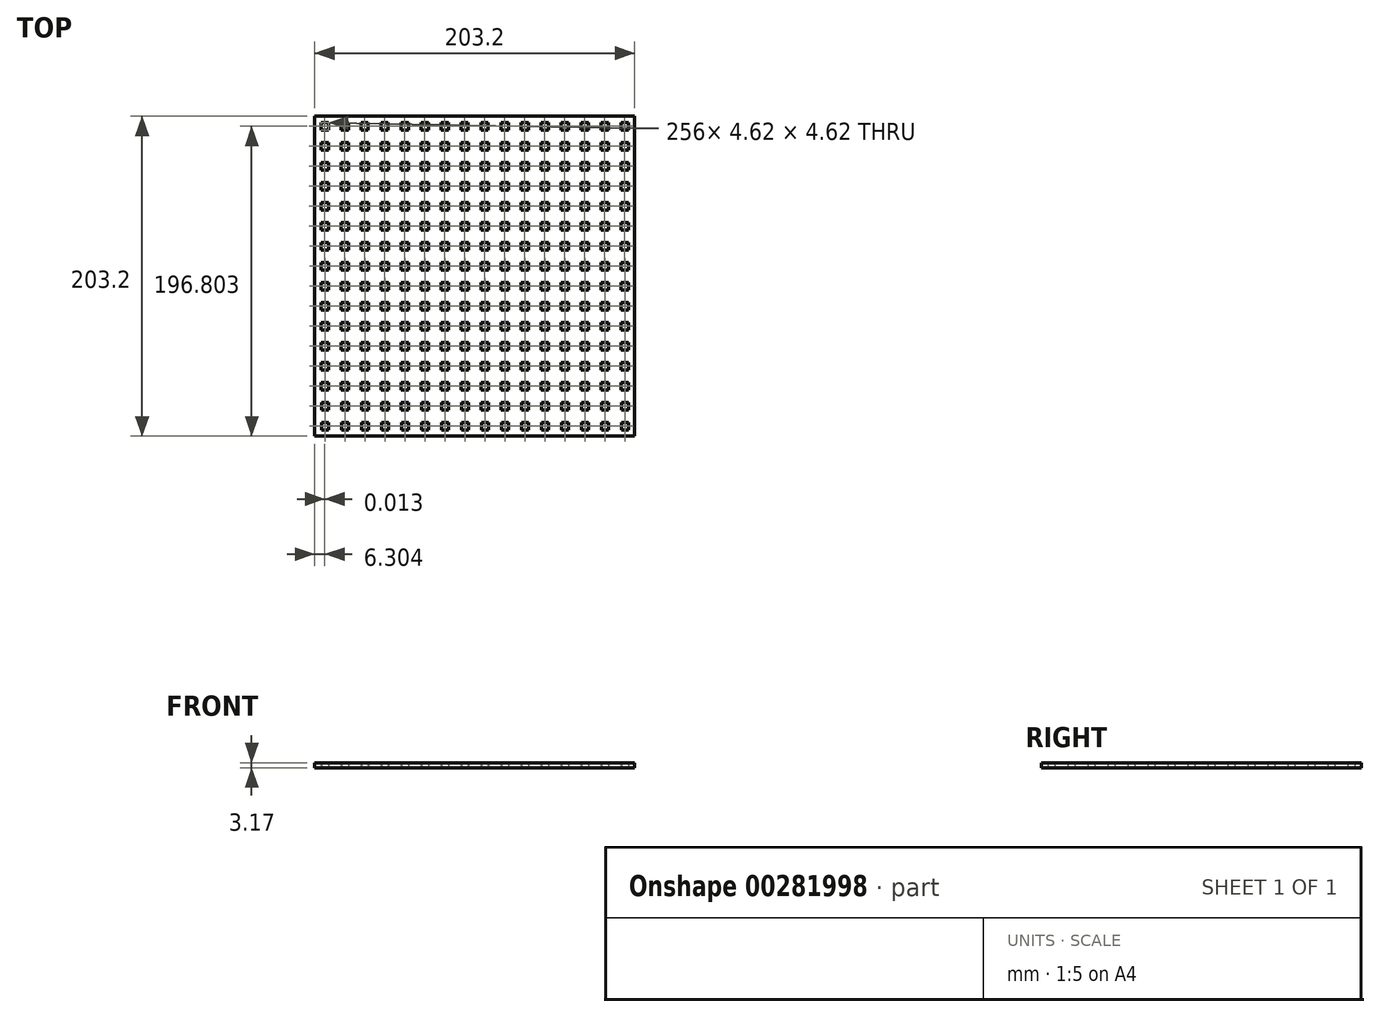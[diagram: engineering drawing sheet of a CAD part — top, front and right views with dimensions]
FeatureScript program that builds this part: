
annotation { "Feature Type Name" : "Feature", "Feature Type Description" : "" }
export const myFeature = defineFeature(function(context is Context, id is Id, definition is map)
    precondition{}
    {
        {
            var Q0;
            Q0=qCreatedBy(makeId("Top.planeOp"),FACE);
            var sketch = newSketch(context, id + "F0", { "sketchPlane" : qUnion([Q0])});
            skLineSegment(sketch, "E0.bottom", {"start": v(-83.26, 106.61) * mm, "end": v(119.94, 106.61) * mm});
            skLineSegment(sketch, "E0.top", {"start": v(-83.26, -96.59) * mm, "end": v(119.94, -96.59) * mm});
            skLineSegment(sketch, "E0.left", {"start": v(-83.26, 106.61) * mm, "end": v(-83.26, -96.59) * mm});
            skLineSegment(sketch, "E0.right", {"start": v(119.94, 106.61) * mm, "end": v(119.94, -96.59) * mm});
            skPoint(sketch, "E1", {"position": v(-79.27, 106.61) * mm});
            skPoint(sketch, "E2", {"position": v(-83.26, 102.52) * mm});
            skLineSegment(sketch, "E3.bottom", {"start": v(-79.27, 102.52) * mm, "end": v(-74.64, 102.52) * mm});
            skLineSegment(sketch, "E3.top", {"start": v(-79.27, 97.9) * mm, "end": v(-74.64, 97.9) * mm});
            skLineSegment(sketch, "E3.left", {"start": v(-79.27, 102.52) * mm, "end": v(-79.27, 97.9) * mm});
            skLineSegment(sketch, "E3.right", {"start": v(-74.64, 102.52) * mm, "end": v(-74.64, 97.9) * mm});
            skPoint(sketch, "E4", {"position": v(-76.96, 102.52) * mm});
            skPoint(sketch, "E5", {"position": v(-64.26, 102.52) * mm});
            skLineSegment(sketch, "E6.bottom", {"start": v(-66.57, 102.52) * mm, "end": v(-61.94, 102.52) * mm});
            skLineSegment(sketch, "E6.top", {"start": v(-66.57, 97.9) * mm, "end": v(-61.94, 97.9) * mm});
            skLineSegment(sketch, "E6.left", {"start": v(-66.57, 102.52) * mm, "end": v(-66.57, 97.9) * mm});
            skLineSegment(sketch, "E6.right", {"start": v(-61.94, 102.52) * mm, "end": v(-61.94, 97.9) * mm});
            skLineSegment(sketch, "E7.1.0.0", {"start": v(-53.87, 97.9) * mm, "end": v(-49.24, 97.9) * mm});
            skLineSegment(sketch, "E7.1.0.1", {"start": v(-36.54, 102.52) * mm, "end": v(-36.54, 97.9) * mm});
            skLineSegment(sketch, "E7.1.0.2", {"start": v(-41.17, 97.9) * mm, "end": v(-36.54, 97.9) * mm});
            skLineSegment(sketch, "E7.1.0.3", {"start": v(-41.17, 102.52) * mm, "end": v(-41.17, 97.9) * mm});
            skPoint(sketch, "E7.1.0.4", {"position": v(-51.56, 102.52) * mm});
            skPoint(sketch, "E7.1.0.5", {"position": v(-38.86, 102.52) * mm});
            skLineSegment(sketch, "E7.1.0.6", {"start": v(-53.87, 102.52) * mm, "end": v(-53.87, 97.9) * mm});
            skLineSegment(sketch, "E7.1.0.7", {"start": v(-49.24, 102.52) * mm, "end": v(-49.24, 97.9) * mm});
            skLineSegment(sketch, "E7.1.0.8", {"start": v(-41.17, 102.52) * mm, "end": v(-36.54, 102.52) * mm});
            skLineSegment(sketch, "E7.1.0.9", {"start": v(-53.87, 102.52) * mm, "end": v(-49.24, 102.52) * mm});
            skLineSegment(sketch, "E7.2.0.0", {"start": v(-28.47, 97.9) * mm, "end": v(-23.84, 97.9) * mm});
            skLineSegment(sketch, "E7.2.0.1", {"start": v(-11.14, 102.52) * mm, "end": v(-11.14, 97.9) * mm});
            skLineSegment(sketch, "E7.2.0.2", {"start": v(-15.77, 97.9) * mm, "end": v(-11.14, 97.9) * mm});
            skLineSegment(sketch, "E7.2.0.3", {"start": v(-15.77, 102.52) * mm, "end": v(-15.77, 97.9) * mm});
            skPoint(sketch, "E7.2.0.4", {"position": v(-26.16, 102.52) * mm});
            skPoint(sketch, "E7.2.0.5", {"position": v(-13.46, 102.52) * mm});
            skLineSegment(sketch, "E7.2.0.6", {"start": v(-28.47, 102.52) * mm, "end": v(-28.47, 97.9) * mm});
            skLineSegment(sketch, "E7.2.0.7", {"start": v(-23.84, 102.52) * mm, "end": v(-23.84, 97.9) * mm});
            skLineSegment(sketch, "E7.2.0.8", {"start": v(-15.77, 102.52) * mm, "end": v(-11.14, 102.52) * mm});
            skLineSegment(sketch, "E7.2.0.9", {"start": v(-28.47, 102.52) * mm, "end": v(-23.84, 102.52) * mm});
            skLineSegment(sketch, "E7.3.0.0", {"start": v(-3.07, 97.9) * mm, "end": v(1.56, 97.9) * mm});
            skLineSegment(sketch, "E7.3.0.1", {"start": v(14.26, 102.52) * mm, "end": v(14.26, 97.9) * mm});
            skLineSegment(sketch, "E7.3.0.2", {"start": v(9.63, 97.9) * mm, "end": v(14.26, 97.9) * mm});
            skLineSegment(sketch, "E7.3.0.3", {"start": v(9.63, 102.52) * mm, "end": v(9.63, 97.9) * mm});
            skPoint(sketch, "E7.3.0.4", {"position": v(-0.76, 102.52) * mm});
            skPoint(sketch, "E7.3.0.5", {"position": v(11.94, 102.52) * mm});
            skLineSegment(sketch, "E7.3.0.6", {"start": v(-3.07, 102.52) * mm, "end": v(-3.07, 97.9) * mm});
            skLineSegment(sketch, "E7.3.0.7", {"start": v(1.56, 102.52) * mm, "end": v(1.56, 97.9) * mm});
            skLineSegment(sketch, "E7.3.0.8", {"start": v(9.63, 102.52) * mm, "end": v(14.26, 102.52) * mm});
            skLineSegment(sketch, "E7.3.0.9", {"start": v(-3.07, 102.52) * mm, "end": v(1.56, 102.52) * mm});
            skLineSegment(sketch, "E7.4.0.0", {"start": v(22.33, 97.9) * mm, "end": v(26.96, 97.9) * mm});
            skLineSegment(sketch, "E7.4.0.1", {"start": v(39.66, 102.52) * mm, "end": v(39.66, 97.9) * mm});
            skLineSegment(sketch, "E7.4.0.2", {"start": v(35.03, 97.9) * mm, "end": v(39.66, 97.9) * mm});
            skLineSegment(sketch, "E7.4.0.3", {"start": v(35.03, 102.52) * mm, "end": v(35.03, 97.9) * mm});
            skPoint(sketch, "E7.4.0.4", {"position": v(24.64, 102.52) * mm});
            skPoint(sketch, "E7.4.0.5", {"position": v(37.34, 102.52) * mm});
            skLineSegment(sketch, "E7.4.0.6", {"start": v(22.33, 102.52) * mm, "end": v(22.33, 97.9) * mm});
            skLineSegment(sketch, "E7.4.0.7", {"start": v(26.96, 102.52) * mm, "end": v(26.96, 97.9) * mm});
            skLineSegment(sketch, "E7.4.0.8", {"start": v(35.03, 102.52) * mm, "end": v(39.66, 102.52) * mm});
            skLineSegment(sketch, "E7.4.0.9", {"start": v(22.33, 102.52) * mm, "end": v(26.96, 102.52) * mm});
            skLineSegment(sketch, "E7.5.0.0", {"start": v(47.73, 97.9) * mm, "end": v(52.36, 97.9) * mm});
            skLineSegment(sketch, "E7.5.0.1", {"start": v(65.06, 102.52) * mm, "end": v(65.06, 97.9) * mm});
            skLineSegment(sketch, "E7.5.0.2", {"start": v(60.43, 97.9) * mm, "end": v(65.06, 97.9) * mm});
            skLineSegment(sketch, "E7.5.0.3", {"start": v(60.43, 102.52) * mm, "end": v(60.43, 97.9) * mm});
            skPoint(sketch, "E7.5.0.4", {"position": v(50.04, 102.52) * mm});
            skPoint(sketch, "E7.5.0.5", {"position": v(62.74, 102.52) * mm});
            skLineSegment(sketch, "E7.5.0.6", {"start": v(47.73, 102.52) * mm, "end": v(47.73, 97.9) * mm});
            skLineSegment(sketch, "E7.5.0.7", {"start": v(52.36, 102.52) * mm, "end": v(52.36, 97.9) * mm});
            skLineSegment(sketch, "E7.5.0.8", {"start": v(60.43, 102.52) * mm, "end": v(65.06, 102.52) * mm});
            skLineSegment(sketch, "E7.5.0.9", {"start": v(47.73, 102.52) * mm, "end": v(52.36, 102.52) * mm});
            skLineSegment(sketch, "E7.6.0.0", {"start": v(73.13, 97.9) * mm, "end": v(77.76, 97.9) * mm});
            skLineSegment(sketch, "E7.6.0.1", {"start": v(90.46, 102.52) * mm, "end": v(90.46, 97.9) * mm});
            skLineSegment(sketch, "E7.6.0.2", {"start": v(85.83, 97.9) * mm, "end": v(90.46, 97.9) * mm});
            skLineSegment(sketch, "E7.6.0.3", {"start": v(85.83, 102.52) * mm, "end": v(85.83, 97.9) * mm});
            skPoint(sketch, "E7.6.0.4", {"position": v(75.44, 102.52) * mm});
            skPoint(sketch, "E7.6.0.5", {"position": v(88.14, 102.52) * mm});
            skLineSegment(sketch, "E7.6.0.6", {"start": v(73.13, 102.52) * mm, "end": v(73.13, 97.9) * mm});
            skLineSegment(sketch, "E7.6.0.7", {"start": v(77.76, 102.52) * mm, "end": v(77.76, 97.9) * mm});
            skLineSegment(sketch, "E7.6.0.8", {"start": v(85.83, 102.52) * mm, "end": v(90.46, 102.52) * mm});
            skLineSegment(sketch, "E7.6.0.9", {"start": v(73.13, 102.52) * mm, "end": v(77.76, 102.52) * mm});
            skLineSegment(sketch, "E7.7.0.0", {"start": v(98.53, 97.9) * mm, "end": v(103.16, 97.9) * mm});
            skLineSegment(sketch, "E7.7.0.1", {"start": v(115.86, 102.52) * mm, "end": v(115.86, 97.9) * mm});
            skLineSegment(sketch, "E7.7.0.2", {"start": v(111.23, 97.9) * mm, "end": v(115.86, 97.9) * mm});
            skLineSegment(sketch, "E7.7.0.3", {"start": v(111.23, 102.52) * mm, "end": v(111.23, 97.9) * mm});
            skPoint(sketch, "E7.7.0.4", {"position": v(100.84, 102.52) * mm});
            skPoint(sketch, "E7.7.0.5", {"position": v(113.54, 102.52) * mm});
            skLineSegment(sketch, "E7.7.0.6", {"start": v(98.53, 102.52) * mm, "end": v(98.53, 97.9) * mm});
            skLineSegment(sketch, "E7.7.0.7", {"start": v(103.16, 102.52) * mm, "end": v(103.16, 97.9) * mm});
            skLineSegment(sketch, "E7.7.0.8", {"start": v(111.23, 102.52) * mm, "end": v(115.86, 102.52) * mm});
            skLineSegment(sketch, "E7.7.0.9", {"start": v(98.53, 102.52) * mm, "end": v(103.16, 102.52) * mm});
            skLineSegment(sketch, "E7.direction1", {"start": v(-76.96, 102.52) * mm, "end": v(-51.56, 102.52) * mm, "construction": true});
            skPoint(sketch, "E8", {"position": v(-79.27, 100.21) * mm});
            skPoint(sketch, "E9.1.0.0", {"position": v(-79.25, 87.51) * mm});
            skPoint(sketch, "E9.1.0.1", {"position": v(88.16, 89.82) * mm});
            skPoint(sketch, "E9.1.0.2", {"position": v(37.36, 89.82) * mm});
            skPoint(sketch, "E9.1.0.3", {"position": v(-51.54, 89.82) * mm});
            skPoint(sketch, "E9.1.0.4", {"position": v(113.56, 89.82) * mm});
            skPoint(sketch, "E9.1.0.5", {"position": v(-64.24, 89.82) * mm});
            skPoint(sketch, "E9.1.0.6", {"position": v(24.66, 89.82) * mm});
            skPoint(sketch, "E9.1.0.7", {"position": v(11.96, 89.82) * mm});
            skLineSegment(sketch, "E9.1.0.8", {"start": v(-76.94, 89.82) * mm, "end": v(-51.54, 89.82) * mm, "construction": true});
            skPoint(sketch, "E9.1.0.9", {"position": v(-76.94, 89.82) * mm});
            skPoint(sketch, "E9.1.0.10", {"position": v(-13.44, 89.82) * mm});
            skPoint(sketch, "E9.1.0.11", {"position": v(50.06, 89.82) * mm});
            skPoint(sketch, "E9.1.0.12", {"position": v(-38.84, 89.82) * mm});
            skPoint(sketch, "E9.1.0.13", {"position": v(62.76, 89.82) * mm});
            skPoint(sketch, "E9.1.0.14", {"position": v(-26.14, 89.82) * mm});
            skPoint(sketch, "E9.1.0.15", {"position": v(75.46, 89.82) * mm});
            skPoint(sketch, "E9.1.0.16", {"position": v(-0.74, 89.82) * mm});
            skPoint(sketch, "E9.1.0.17", {"position": v(100.86, 89.82) * mm});
            skLineSegment(sketch, "E9.1.0.18", {"start": v(90.47, 89.82) * mm, "end": v(90.47, 85.2) * mm});
            skLineSegment(sketch, "E9.1.0.19", {"start": v(47.75, 89.82) * mm, "end": v(47.75, 85.2) * mm});
            skLineSegment(sketch, "E9.1.0.20", {"start": v(-28.45, 89.82) * mm, "end": v(-28.45, 85.2) * mm});
            skLineSegment(sketch, "E9.1.0.21", {"start": v(73.15, 89.82) * mm, "end": v(73.15, 85.2) * mm});
            skLineSegment(sketch, "E9.1.0.22", {"start": v(9.65, 85.2) * mm, "end": v(14.27, 85.2) * mm});
            skLineSegment(sketch, "E9.1.0.23", {"start": v(98.55, 89.82) * mm, "end": v(98.55, 85.2) * mm});
            skLineSegment(sketch, "E9.1.0.24", {"start": v(39.67, 89.82) * mm, "end": v(39.67, 85.2) * mm});
            skLineSegment(sketch, "E9.1.0.25", {"start": v(-15.75, 89.82) * mm, "end": v(-15.75, 85.2) * mm});
            skLineSegment(sketch, "E9.1.0.26", {"start": v(60.45, 85.2) * mm, "end": v(65.07, 85.2) * mm});
            skLineSegment(sketch, "E9.1.0.27", {"start": v(35.05, 89.82) * mm, "end": v(35.05, 85.2) * mm});
            skLineSegment(sketch, "E9.1.0.28", {"start": v(85.85, 89.82) * mm, "end": v(85.85, 85.2) * mm});
            skLineSegment(sketch, "E9.1.0.29", {"start": v(-53.85, 85.2) * mm, "end": v(-49.23, 85.2) * mm});
            skLineSegment(sketch, "E9.1.0.30", {"start": v(-66.55, 89.82) * mm, "end": v(-61.93, 89.82) * mm});
            skLineSegment(sketch, "E9.1.0.31", {"start": v(111.25, 85.2) * mm, "end": v(115.87, 85.2) * mm});
            skLineSegment(sketch, "E9.1.0.32", {"start": v(-74.63, 89.82) * mm, "end": v(-74.63, 85.2) * mm});
            skLineSegment(sketch, "E9.1.0.33", {"start": v(-79.25, 89.82) * mm, "end": v(-79.25, 85.2) * mm});
            skLineSegment(sketch, "E9.1.0.34", {"start": v(-79.25, 89.82) * mm, "end": v(-74.63, 89.82) * mm});
            skLineSegment(sketch, "E9.1.0.35", {"start": v(-41.15, 89.82) * mm, "end": v(-41.15, 85.2) * mm});
            skLineSegment(sketch, "E9.1.0.36", {"start": v(-11.13, 89.82) * mm, "end": v(-11.13, 85.2) * mm});
            skLineSegment(sketch, "E9.1.0.37", {"start": v(-3.05, 85.2) * mm, "end": v(1.57, 85.2) * mm});
            skLineSegment(sketch, "E9.1.0.38", {"start": v(47.75, 85.2) * mm, "end": v(52.37, 85.2) * mm});
            skLineSegment(sketch, "E9.1.0.39", {"start": v(98.55, 85.2) * mm, "end": v(103.17, 85.2) * mm});
            skLineSegment(sketch, "E9.1.0.40", {"start": v(9.65, 89.82) * mm, "end": v(14.27, 89.82) * mm});
            skLineSegment(sketch, "E9.1.0.41", {"start": v(14.27, 89.82) * mm, "end": v(14.27, 85.2) * mm});
            skLineSegment(sketch, "E9.1.0.42", {"start": v(22.35, 85.2) * mm, "end": v(26.97, 85.2) * mm});
            skLineSegment(sketch, "E9.1.0.43", {"start": v(73.15, 85.2) * mm, "end": v(77.77, 85.2) * mm});
            skLineSegment(sketch, "E9.1.0.44", {"start": v(115.87, 89.82) * mm, "end": v(115.87, 85.2) * mm});
            skLineSegment(sketch, "E9.1.0.45", {"start": v(60.45, 89.82) * mm, "end": v(65.07, 89.82) * mm});
            skLineSegment(sketch, "E9.1.0.46", {"start": v(111.25, 89.82) * mm, "end": v(115.87, 89.82) * mm});
            skLineSegment(sketch, "E9.1.0.47", {"start": v(-15.75, 89.82) * mm, "end": v(-11.13, 89.82) * mm});
            skLineSegment(sketch, "E9.1.0.48", {"start": v(35.05, 89.82) * mm, "end": v(39.67, 89.82) * mm});
            skLineSegment(sketch, "E9.1.0.49", {"start": v(-23.83, 89.82) * mm, "end": v(-23.83, 85.2) * mm});
            skLineSegment(sketch, "E9.1.0.50", {"start": v(85.85, 89.82) * mm, "end": v(90.47, 89.82) * mm});
            skLineSegment(sketch, "E9.1.0.51", {"start": v(65.07, 89.82) * mm, "end": v(65.07, 85.2) * mm});
            skLineSegment(sketch, "E9.1.0.52", {"start": v(52.37, 89.82) * mm, "end": v(52.37, 85.2) * mm});
            skLineSegment(sketch, "E9.1.0.53", {"start": v(103.17, 89.82) * mm, "end": v(103.17, 85.2) * mm});
            skLineSegment(sketch, "E9.1.0.54", {"start": v(-15.75, 85.2) * mm, "end": v(-11.13, 85.2) * mm});
            skLineSegment(sketch, "E9.1.0.55", {"start": v(111.25, 89.82) * mm, "end": v(111.25, 85.2) * mm});
            skLineSegment(sketch, "E9.1.0.56", {"start": v(60.45, 89.82) * mm, "end": v(60.45, 85.2) * mm});
            skLineSegment(sketch, "E9.1.0.57", {"start": v(85.85, 85.2) * mm, "end": v(90.47, 85.2) * mm});
            skLineSegment(sketch, "E9.1.0.58", {"start": v(35.05, 85.2) * mm, "end": v(39.67, 85.2) * mm});
            skLineSegment(sketch, "E9.1.0.59", {"start": v(9.65, 89.82) * mm, "end": v(9.65, 85.2) * mm});
            skLineSegment(sketch, "E9.1.0.60", {"start": v(-36.53, 89.82) * mm, "end": v(-36.53, 85.2) * mm});
            skLineSegment(sketch, "E9.1.0.61", {"start": v(-41.15, 85.2) * mm, "end": v(-36.53, 85.2) * mm});
            skLineSegment(sketch, "E9.1.0.62", {"start": v(-79.25, 85.2) * mm, "end": v(-74.63, 85.2) * mm});
            skLineSegment(sketch, "E9.1.0.63", {"start": v(-66.55, 85.2) * mm, "end": v(-61.93, 85.2) * mm});
            skLineSegment(sketch, "E9.1.0.64", {"start": v(-66.55, 89.82) * mm, "end": v(-66.55, 85.2) * mm});
            skLineSegment(sketch, "E9.1.0.65", {"start": v(-61.93, 89.82) * mm, "end": v(-61.93, 85.2) * mm});
            skLineSegment(sketch, "E9.1.0.66", {"start": v(-53.85, 89.82) * mm, "end": v(-53.85, 85.2) * mm});
            skLineSegment(sketch, "E9.1.0.67", {"start": v(-3.05, 89.82) * mm, "end": v(-3.05, 85.2) * mm});
            skLineSegment(sketch, "E9.1.0.68", {"start": v(22.35, 89.82) * mm, "end": v(22.35, 85.2) * mm});
            skLineSegment(sketch, "E9.1.0.69", {"start": v(-49.23, 89.82) * mm, "end": v(-49.23, 85.2) * mm});
            skLineSegment(sketch, "E9.1.0.70", {"start": v(1.57, 89.82) * mm, "end": v(1.57, 85.2) * mm});
            skLineSegment(sketch, "E9.1.0.71", {"start": v(77.77, 89.82) * mm, "end": v(77.77, 85.2) * mm});
            skLineSegment(sketch, "E9.1.0.72", {"start": v(26.97, 89.82) * mm, "end": v(26.97, 85.2) * mm});
            skLineSegment(sketch, "E9.1.0.73", {"start": v(-41.15, 89.82) * mm, "end": v(-36.53, 89.82) * mm});
            skLineSegment(sketch, "E9.1.0.74", {"start": v(-28.45, 85.2) * mm, "end": v(-23.83, 85.2) * mm});
            skLineSegment(sketch, "E9.1.0.75", {"start": v(-28.45, 89.82) * mm, "end": v(-23.83, 89.82) * mm});
            skLineSegment(sketch, "E9.1.0.76", {"start": v(22.35, 89.82) * mm, "end": v(26.97, 89.82) * mm});
            skLineSegment(sketch, "E9.1.0.77", {"start": v(73.15, 89.82) * mm, "end": v(77.77, 89.82) * mm});
            skLineSegment(sketch, "E9.1.0.78", {"start": v(-3.05, 89.82) * mm, "end": v(1.57, 89.82) * mm});
            skLineSegment(sketch, "E9.1.0.79", {"start": v(47.75, 89.82) * mm, "end": v(52.37, 89.82) * mm});
            skLineSegment(sketch, "E9.1.0.80", {"start": v(98.55, 89.82) * mm, "end": v(103.17, 89.82) * mm});
            skLineSegment(sketch, "E9.1.0.81", {"start": v(-53.85, 89.82) * mm, "end": v(-49.23, 89.82) * mm});
            skPoint(sketch, "E9.2.0.0", {"position": v(-79.24, 74.81) * mm});
            skPoint(sketch, "E9.2.0.1", {"position": v(88.17, 77.12) * mm});
            skPoint(sketch, "E9.2.0.2", {"position": v(37.37, 77.12) * mm});
            skPoint(sketch, "E9.2.0.3", {"position": v(-51.53, 77.12) * mm});
            skPoint(sketch, "E9.2.0.4", {"position": v(113.57, 77.12) * mm});
            skPoint(sketch, "E9.2.0.5", {"position": v(-64.23, 77.12) * mm});
            skPoint(sketch, "E9.2.0.6", {"position": v(24.67, 77.12) * mm});
            skPoint(sketch, "E9.2.0.7", {"position": v(11.97, 77.12) * mm});
            skLineSegment(sketch, "E9.2.0.8", {"start": v(-76.93, 77.12) * mm, "end": v(-51.53, 77.12) * mm, "construction": true});
            skPoint(sketch, "E9.2.0.9", {"position": v(-76.93, 77.12) * mm});
            skPoint(sketch, "E9.2.0.10", {"position": v(-13.43, 77.12) * mm});
            skPoint(sketch, "E9.2.0.11", {"position": v(50.07, 77.12) * mm});
            skPoint(sketch, "E9.2.0.12", {"position": v(-38.83, 77.12) * mm});
            skPoint(sketch, "E9.2.0.13", {"position": v(62.77, 77.12) * mm});
            skPoint(sketch, "E9.2.0.14", {"position": v(-26.13, 77.12) * mm});
            skPoint(sketch, "E9.2.0.15", {"position": v(75.47, 77.12) * mm});
            skPoint(sketch, "E9.2.0.16", {"position": v(-0.73, 77.12) * mm});
            skPoint(sketch, "E9.2.0.17", {"position": v(100.87, 77.12) * mm});
            skLineSegment(sketch, "E9.2.0.18", {"start": v(90.48, 77.12) * mm, "end": v(90.48, 72.5) * mm});
            skLineSegment(sketch, "E9.2.0.19", {"start": v(47.76, 77.12) * mm, "end": v(47.76, 72.5) * mm});
            skLineSegment(sketch, "E9.2.0.20", {"start": v(-28.44, 77.12) * mm, "end": v(-28.44, 72.5) * mm});
            skLineSegment(sketch, "E9.2.0.21", {"start": v(73.16, 77.12) * mm, "end": v(73.16, 72.5) * mm});
            skLineSegment(sketch, "E9.2.0.22", {"start": v(9.66, 72.5) * mm, "end": v(14.28, 72.5) * mm});
            skLineSegment(sketch, "E9.2.0.23", {"start": v(98.56, 77.12) * mm, "end": v(98.56, 72.5) * mm});
            skLineSegment(sketch, "E9.2.0.24", {"start": v(39.68, 77.12) * mm, "end": v(39.68, 72.5) * mm});
            skLineSegment(sketch, "E9.2.0.25", {"start": v(-15.74, 77.12) * mm, "end": v(-15.74, 72.5) * mm});
            skLineSegment(sketch, "E9.2.0.26", {"start": v(60.46, 72.5) * mm, "end": v(65.08, 72.5) * mm});
            skLineSegment(sketch, "E9.2.0.27", {"start": v(35.06, 77.12) * mm, "end": v(35.06, 72.5) * mm});
            skLineSegment(sketch, "E9.2.0.28", {"start": v(85.86, 77.12) * mm, "end": v(85.86, 72.5) * mm});
            skLineSegment(sketch, "E9.2.0.29", {"start": v(-53.84, 72.5) * mm, "end": v(-49.22, 72.5) * mm});
            skLineSegment(sketch, "E9.2.0.30", {"start": v(-66.54, 77.12) * mm, "end": v(-61.92, 77.12) * mm});
            skLineSegment(sketch, "E9.2.0.31", {"start": v(111.26, 72.5) * mm, "end": v(115.88, 72.5) * mm});
            skLineSegment(sketch, "E9.2.0.32", {"start": v(-74.62, 77.12) * mm, "end": v(-74.62, 72.5) * mm});
            skLineSegment(sketch, "E9.2.0.33", {"start": v(-79.24, 77.12) * mm, "end": v(-79.24, 72.5) * mm});
            skLineSegment(sketch, "E9.2.0.34", {"start": v(-79.24, 77.12) * mm, "end": v(-74.62, 77.12) * mm});
            skLineSegment(sketch, "E9.2.0.35", {"start": v(-41.14, 77.12) * mm, "end": v(-41.14, 72.5) * mm});
            skLineSegment(sketch, "E9.2.0.36", {"start": v(-11.12, 77.12) * mm, "end": v(-11.12, 72.5) * mm});
            skLineSegment(sketch, "E9.2.0.37", {"start": v(-3.04, 72.5) * mm, "end": v(1.58, 72.5) * mm});
            skLineSegment(sketch, "E9.2.0.38", {"start": v(47.76, 72.5) * mm, "end": v(52.38, 72.5) * mm});
            skLineSegment(sketch, "E9.2.0.39", {"start": v(98.56, 72.5) * mm, "end": v(103.18, 72.5) * mm});
            skLineSegment(sketch, "E9.2.0.40", {"start": v(9.66, 77.12) * mm, "end": v(14.28, 77.12) * mm});
            skLineSegment(sketch, "E9.2.0.41", {"start": v(14.28, 77.12) * mm, "end": v(14.28, 72.5) * mm});
            skLineSegment(sketch, "E9.2.0.42", {"start": v(22.36, 72.5) * mm, "end": v(26.98, 72.5) * mm});
            skLineSegment(sketch, "E9.2.0.43", {"start": v(73.16, 72.5) * mm, "end": v(77.78, 72.5) * mm});
            skLineSegment(sketch, "E9.2.0.44", {"start": v(115.88, 77.12) * mm, "end": v(115.88, 72.5) * mm});
            skLineSegment(sketch, "E9.2.0.45", {"start": v(60.46, 77.12) * mm, "end": v(65.08, 77.12) * mm});
            skLineSegment(sketch, "E9.2.0.46", {"start": v(111.26, 77.12) * mm, "end": v(115.88, 77.12) * mm});
            skLineSegment(sketch, "E9.2.0.47", {"start": v(-15.74, 77.12) * mm, "end": v(-11.12, 77.12) * mm});
            skLineSegment(sketch, "E9.2.0.48", {"start": v(35.06, 77.12) * mm, "end": v(39.68, 77.12) * mm});
            skLineSegment(sketch, "E9.2.0.49", {"start": v(-23.82, 77.12) * mm, "end": v(-23.82, 72.5) * mm});
            skLineSegment(sketch, "E9.2.0.50", {"start": v(85.86, 77.12) * mm, "end": v(90.48, 77.12) * mm});
            skLineSegment(sketch, "E9.2.0.51", {"start": v(65.08, 77.12) * mm, "end": v(65.08, 72.5) * mm});
            skLineSegment(sketch, "E9.2.0.52", {"start": v(52.38, 77.12) * mm, "end": v(52.38, 72.5) * mm});
            skLineSegment(sketch, "E9.2.0.53", {"start": v(103.18, 77.12) * mm, "end": v(103.18, 72.5) * mm});
            skLineSegment(sketch, "E9.2.0.54", {"start": v(-15.74, 72.5) * mm, "end": v(-11.12, 72.5) * mm});
            skLineSegment(sketch, "E9.2.0.55", {"start": v(111.26, 77.12) * mm, "end": v(111.26, 72.5) * mm});
            skLineSegment(sketch, "E9.2.0.56", {"start": v(60.46, 77.12) * mm, "end": v(60.46, 72.5) * mm});
            skLineSegment(sketch, "E9.2.0.57", {"start": v(85.86, 72.5) * mm, "end": v(90.48, 72.5) * mm});
            skLineSegment(sketch, "E9.2.0.58", {"start": v(35.06, 72.5) * mm, "end": v(39.68, 72.5) * mm});
            skLineSegment(sketch, "E9.2.0.59", {"start": v(9.66, 77.12) * mm, "end": v(9.66, 72.5) * mm});
            skLineSegment(sketch, "E9.2.0.60", {"start": v(-36.52, 77.12) * mm, "end": v(-36.52, 72.5) * mm});
            skLineSegment(sketch, "E9.2.0.61", {"start": v(-41.14, 72.5) * mm, "end": v(-36.52, 72.5) * mm});
            skLineSegment(sketch, "E9.2.0.62", {"start": v(-79.24, 72.5) * mm, "end": v(-74.62, 72.5) * mm});
            skLineSegment(sketch, "E9.2.0.63", {"start": v(-66.54, 72.5) * mm, "end": v(-61.92, 72.5) * mm});
            skLineSegment(sketch, "E9.2.0.64", {"start": v(-66.54, 77.12) * mm, "end": v(-66.54, 72.5) * mm});
            skLineSegment(sketch, "E9.2.0.65", {"start": v(-61.92, 77.12) * mm, "end": v(-61.92, 72.5) * mm});
            skLineSegment(sketch, "E9.2.0.66", {"start": v(-53.84, 77.12) * mm, "end": v(-53.84, 72.5) * mm});
            skLineSegment(sketch, "E9.2.0.67", {"start": v(-3.04, 77.12) * mm, "end": v(-3.04, 72.5) * mm});
            skLineSegment(sketch, "E9.2.0.68", {"start": v(22.36, 77.12) * mm, "end": v(22.36, 72.5) * mm});
            skLineSegment(sketch, "E9.2.0.69", {"start": v(-49.22, 77.12) * mm, "end": v(-49.22, 72.5) * mm});
            skLineSegment(sketch, "E9.2.0.70", {"start": v(1.58, 77.12) * mm, "end": v(1.58, 72.5) * mm});
            skLineSegment(sketch, "E9.2.0.71", {"start": v(77.78, 77.12) * mm, "end": v(77.78, 72.5) * mm});
            skLineSegment(sketch, "E9.2.0.72", {"start": v(26.98, 77.12) * mm, "end": v(26.98, 72.5) * mm});
            skLineSegment(sketch, "E9.2.0.73", {"start": v(-41.14, 77.12) * mm, "end": v(-36.52, 77.12) * mm});
            skLineSegment(sketch, "E9.2.0.74", {"start": v(-28.44, 72.5) * mm, "end": v(-23.82, 72.5) * mm});
            skLineSegment(sketch, "E9.2.0.75", {"start": v(-28.44, 77.12) * mm, "end": v(-23.82, 77.12) * mm});
            skLineSegment(sketch, "E9.2.0.76", {"start": v(22.36, 77.12) * mm, "end": v(26.98, 77.12) * mm});
            skLineSegment(sketch, "E9.2.0.77", {"start": v(73.16, 77.12) * mm, "end": v(77.78, 77.12) * mm});
            skLineSegment(sketch, "E9.2.0.78", {"start": v(-3.04, 77.12) * mm, "end": v(1.58, 77.12) * mm});
            skLineSegment(sketch, "E9.2.0.79", {"start": v(47.76, 77.12) * mm, "end": v(52.38, 77.12) * mm});
            skLineSegment(sketch, "E9.2.0.80", {"start": v(98.56, 77.12) * mm, "end": v(103.18, 77.12) * mm});
            skLineSegment(sketch, "E9.2.0.81", {"start": v(-53.84, 77.12) * mm, "end": v(-49.22, 77.12) * mm});
            skPoint(sketch, "E9.3.0.0", {"position": v(-79.23, 62.11) * mm});
            skPoint(sketch, "E9.3.0.1", {"position": v(88.18, 64.42) * mm});
            skPoint(sketch, "E9.3.0.2", {"position": v(37.38, 64.42) * mm});
            skPoint(sketch, "E9.3.0.3", {"position": v(-51.52, 64.42) * mm});
            skPoint(sketch, "E9.3.0.4", {"position": v(113.58, 64.42) * mm});
            skPoint(sketch, "E9.3.0.5", {"position": v(-64.22, 64.42) * mm});
            skPoint(sketch, "E9.3.0.6", {"position": v(24.68, 64.42) * mm});
            skPoint(sketch, "E9.3.0.7", {"position": v(11.98, 64.42) * mm});
            skLineSegment(sketch, "E9.3.0.8", {"start": v(-76.92, 64.42) * mm, "end": v(-51.52, 64.42) * mm, "construction": true});
            skPoint(sketch, "E9.3.0.9", {"position": v(-76.92, 64.42) * mm});
            skPoint(sketch, "E9.3.0.10", {"position": v(-13.42, 64.42) * mm});
            skPoint(sketch, "E9.3.0.11", {"position": v(50.08, 64.42) * mm});
            skPoint(sketch, "E9.3.0.12", {"position": v(-38.82, 64.42) * mm});
            skPoint(sketch, "E9.3.0.13", {"position": v(62.78, 64.42) * mm});
            skPoint(sketch, "E9.3.0.14", {"position": v(-26.12, 64.42) * mm});
            skPoint(sketch, "E9.3.0.15", {"position": v(75.48, 64.42) * mm});
            skPoint(sketch, "E9.3.0.16", {"position": v(-0.72, 64.42) * mm});
            skPoint(sketch, "E9.3.0.17", {"position": v(100.88, 64.42) * mm});
            skLineSegment(sketch, "E9.3.0.18", {"start": v(90.5, 64.42) * mm, "end": v(90.5, 59.8) * mm});
            skLineSegment(sketch, "E9.3.0.19", {"start": v(47.77, 64.42) * mm, "end": v(47.77, 59.8) * mm});
            skLineSegment(sketch, "E9.3.0.20", {"start": v(-28.43, 64.42) * mm, "end": v(-28.43, 59.8) * mm});
            skLineSegment(sketch, "E9.3.0.21", {"start": v(73.17, 64.42) * mm, "end": v(73.17, 59.8) * mm});
            skLineSegment(sketch, "E9.3.0.22", {"start": v(9.67, 59.8) * mm, "end": v(14.3, 59.8) * mm});
            skLineSegment(sketch, "E9.3.0.23", {"start": v(98.57, 64.42) * mm, "end": v(98.57, 59.8) * mm});
            skLineSegment(sketch, "E9.3.0.24", {"start": v(39.7, 64.42) * mm, "end": v(39.7, 59.8) * mm});
            skLineSegment(sketch, "E9.3.0.25", {"start": v(-15.73, 64.42) * mm, "end": v(-15.73, 59.8) * mm});
            skLineSegment(sketch, "E9.3.0.26", {"start": v(60.47, 59.8) * mm, "end": v(65.1, 59.8) * mm});
            skLineSegment(sketch, "E9.3.0.27", {"start": v(35.07, 64.42) * mm, "end": v(35.07, 59.8) * mm});
            skLineSegment(sketch, "E9.3.0.28", {"start": v(85.87, 64.42) * mm, "end": v(85.87, 59.8) * mm});
            skLineSegment(sketch, "E9.3.0.29", {"start": v(-53.83, 59.8) * mm, "end": v(-49.2, 59.8) * mm});
            skLineSegment(sketch, "E9.3.0.30", {"start": v(-66.53, 64.42) * mm, "end": v(-61.9, 64.42) * mm});
            skLineSegment(sketch, "E9.3.0.31", {"start": v(111.27, 59.8) * mm, "end": v(115.9, 59.8) * mm});
            skLineSegment(sketch, "E9.3.0.32", {"start": v(-74.6, 64.42) * mm, "end": v(-74.6, 59.8) * mm});
            skLineSegment(sketch, "E9.3.0.33", {"start": v(-79.23, 64.42) * mm, "end": v(-79.23, 59.8) * mm});
            skLineSegment(sketch, "E9.3.0.34", {"start": v(-79.23, 64.42) * mm, "end": v(-74.6, 64.42) * mm});
            skLineSegment(sketch, "E9.3.0.35", {"start": v(-41.13, 64.42) * mm, "end": v(-41.13, 59.8) * mm});
            skLineSegment(sketch, "E9.3.0.36", {"start": v(-11.1, 64.42) * mm, "end": v(-11.1, 59.8) * mm});
            skLineSegment(sketch, "E9.3.0.37", {"start": v(-3.03, 59.8) * mm, "end": v(1.6, 59.8) * mm});
            skLineSegment(sketch, "E9.3.0.38", {"start": v(47.77, 59.8) * mm, "end": v(52.4, 59.8) * mm});
            skLineSegment(sketch, "E9.3.0.39", {"start": v(98.57, 59.8) * mm, "end": v(103.2, 59.8) * mm});
            skLineSegment(sketch, "E9.3.0.40", {"start": v(9.67, 64.42) * mm, "end": v(14.3, 64.42) * mm});
            skLineSegment(sketch, "E9.3.0.41", {"start": v(14.3, 64.42) * mm, "end": v(14.3, 59.8) * mm});
            skLineSegment(sketch, "E9.3.0.42", {"start": v(22.37, 59.8) * mm, "end": v(27, 59.8) * mm});
            skLineSegment(sketch, "E9.3.0.43", {"start": v(73.17, 59.8) * mm, "end": v(77.8, 59.8) * mm});
            skLineSegment(sketch, "E9.3.0.44", {"start": v(115.9, 64.42) * mm, "end": v(115.9, 59.8) * mm});
            skLineSegment(sketch, "E9.3.0.45", {"start": v(60.47, 64.42) * mm, "end": v(65.1, 64.42) * mm});
            skLineSegment(sketch, "E9.3.0.46", {"start": v(111.27, 64.42) * mm, "end": v(115.9, 64.42) * mm});
            skLineSegment(sketch, "E9.3.0.47", {"start": v(-15.73, 64.42) * mm, "end": v(-11.1, 64.42) * mm});
            skLineSegment(sketch, "E9.3.0.48", {"start": v(35.07, 64.42) * mm, "end": v(39.7, 64.42) * mm});
            skLineSegment(sketch, "E9.3.0.49", {"start": v(-23.8, 64.42) * mm, "end": v(-23.8, 59.8) * mm});
            skLineSegment(sketch, "E9.3.0.50", {"start": v(85.87, 64.42) * mm, "end": v(90.5, 64.42) * mm});
            skLineSegment(sketch, "E9.3.0.51", {"start": v(65.1, 64.42) * mm, "end": v(65.1, 59.8) * mm});
            skLineSegment(sketch, "E9.3.0.52", {"start": v(52.4, 64.42) * mm, "end": v(52.4, 59.8) * mm});
            skLineSegment(sketch, "E9.3.0.53", {"start": v(103.2, 64.42) * mm, "end": v(103.2, 59.8) * mm});
            skLineSegment(sketch, "E9.3.0.54", {"start": v(-15.73, 59.8) * mm, "end": v(-11.1, 59.8) * mm});
            skLineSegment(sketch, "E9.3.0.55", {"start": v(111.27, 64.42) * mm, "end": v(111.27, 59.8) * mm});
            skLineSegment(sketch, "E9.3.0.56", {"start": v(60.47, 64.42) * mm, "end": v(60.47, 59.8) * mm});
            skLineSegment(sketch, "E9.3.0.57", {"start": v(85.87, 59.8) * mm, "end": v(90.5, 59.8) * mm});
            skLineSegment(sketch, "E9.3.0.58", {"start": v(35.07, 59.8) * mm, "end": v(39.7, 59.8) * mm});
            skLineSegment(sketch, "E9.3.0.59", {"start": v(9.67, 64.42) * mm, "end": v(9.67, 59.8) * mm});
            skLineSegment(sketch, "E9.3.0.60", {"start": v(-36.5, 64.42) * mm, "end": v(-36.5, 59.8) * mm});
            skLineSegment(sketch, "E9.3.0.61", {"start": v(-41.13, 59.8) * mm, "end": v(-36.5, 59.8) * mm});
            skLineSegment(sketch, "E9.3.0.62", {"start": v(-79.23, 59.8) * mm, "end": v(-74.6, 59.8) * mm});
            skLineSegment(sketch, "E9.3.0.63", {"start": v(-66.53, 59.8) * mm, "end": v(-61.9, 59.8) * mm});
            skLineSegment(sketch, "E9.3.0.64", {"start": v(-66.53, 64.42) * mm, "end": v(-66.53, 59.8) * mm});
            skLineSegment(sketch, "E9.3.0.65", {"start": v(-61.9, 64.42) * mm, "end": v(-61.9, 59.8) * mm});
            skLineSegment(sketch, "E9.3.0.66", {"start": v(-53.83, 64.42) * mm, "end": v(-53.83, 59.8) * mm});
            skLineSegment(sketch, "E9.3.0.67", {"start": v(-3.03, 64.42) * mm, "end": v(-3.03, 59.8) * mm});
            skLineSegment(sketch, "E9.3.0.68", {"start": v(22.37, 64.42) * mm, "end": v(22.37, 59.8) * mm});
            skLineSegment(sketch, "E9.3.0.69", {"start": v(-49.2, 64.42) * mm, "end": v(-49.2, 59.8) * mm});
            skLineSegment(sketch, "E9.3.0.70", {"start": v(1.6, 64.42) * mm, "end": v(1.6, 59.8) * mm});
            skLineSegment(sketch, "E9.3.0.71", {"start": v(77.8, 64.42) * mm, "end": v(77.8, 59.8) * mm});
            skLineSegment(sketch, "E9.3.0.72", {"start": v(27, 64.42) * mm, "end": v(27, 59.8) * mm});
            skLineSegment(sketch, "E9.3.0.73", {"start": v(-41.13, 64.42) * mm, "end": v(-36.5, 64.42) * mm});
            skLineSegment(sketch, "E9.3.0.74", {"start": v(-28.43, 59.8) * mm, "end": v(-23.8, 59.8) * mm});
            skLineSegment(sketch, "E9.3.0.75", {"start": v(-28.43, 64.42) * mm, "end": v(-23.8, 64.42) * mm});
            skLineSegment(sketch, "E9.3.0.76", {"start": v(22.37, 64.42) * mm, "end": v(27, 64.42) * mm});
            skLineSegment(sketch, "E9.3.0.77", {"start": v(73.17, 64.42) * mm, "end": v(77.8, 64.42) * mm});
            skLineSegment(sketch, "E9.3.0.78", {"start": v(-3.03, 64.42) * mm, "end": v(1.6, 64.42) * mm});
            skLineSegment(sketch, "E9.3.0.79", {"start": v(47.77, 64.42) * mm, "end": v(52.4, 64.42) * mm});
            skLineSegment(sketch, "E9.3.0.80", {"start": v(98.57, 64.42) * mm, "end": v(103.2, 64.42) * mm});
            skLineSegment(sketch, "E9.3.0.81", {"start": v(-53.83, 64.42) * mm, "end": v(-49.2, 64.42) * mm});
            skPoint(sketch, "E9.4.0.0", {"position": v(-79.22, 49.41) * mm});
            skPoint(sketch, "E9.4.0.1", {"position": v(88.2, 51.72) * mm});
            skPoint(sketch, "E9.4.0.2", {"position": v(37.4, 51.72) * mm});
            skPoint(sketch, "E9.4.0.3", {"position": v(-51.5, 51.72) * mm});
            skPoint(sketch, "E9.4.0.4", {"position": v(113.6, 51.72) * mm});
            skPoint(sketch, "E9.4.0.5", {"position": v(-64.2, 51.72) * mm});
            skPoint(sketch, "E9.4.0.6", {"position": v(24.7, 51.72) * mm});
            skPoint(sketch, "E9.4.0.7", {"position": v(12, 51.72) * mm});
            skLineSegment(sketch, "E9.4.0.8", {"start": v(-76.9, 51.72) * mm, "end": v(-51.5, 51.72) * mm, "construction": true});
            skPoint(sketch, "E9.4.0.9", {"position": v(-76.9, 51.72) * mm});
            skPoint(sketch, "E9.4.0.10", {"position": v(-13.4, 51.72) * mm});
            skPoint(sketch, "E9.4.0.11", {"position": v(50.1, 51.72) * mm});
            skPoint(sketch, "E9.4.0.12", {"position": v(-38.8, 51.72) * mm});
            skPoint(sketch, "E9.4.0.13", {"position": v(62.8, 51.72) * mm});
            skPoint(sketch, "E9.4.0.14", {"position": v(-26.1, 51.72) * mm});
            skPoint(sketch, "E9.4.0.15", {"position": v(75.5, 51.72) * mm});
            skPoint(sketch, "E9.4.0.16", {"position": v(-0.7, 51.72) * mm});
            skPoint(sketch, "E9.4.0.17", {"position": v(100.9, 51.72) * mm});
            skLineSegment(sketch, "E9.4.0.18", {"start": v(90.5, 51.72) * mm, "end": v(90.5, 47.1) * mm});
            skLineSegment(sketch, "E9.4.0.19", {"start": v(47.78, 51.72) * mm, "end": v(47.78, 47.1) * mm});
            skLineSegment(sketch, "E9.4.0.20", {"start": v(-28.42, 51.72) * mm, "end": v(-28.42, 47.1) * mm});
            skLineSegment(sketch, "E9.4.0.21", {"start": v(73.18, 51.72) * mm, "end": v(73.18, 47.1) * mm});
            skLineSegment(sketch, "E9.4.0.22", {"start": v(9.68, 47.1) * mm, "end": v(14.3, 47.1) * mm});
            skLineSegment(sketch, "E9.4.0.23", {"start": v(98.58, 51.72) * mm, "end": v(98.58, 47.1) * mm});
            skLineSegment(sketch, "E9.4.0.24", {"start": v(39.7, 51.72) * mm, "end": v(39.7, 47.1) * mm});
            skLineSegment(sketch, "E9.4.0.25", {"start": v(-15.72, 51.72) * mm, "end": v(-15.72, 47.1) * mm});
            skLineSegment(sketch, "E9.4.0.26", {"start": v(60.48, 47.1) * mm, "end": v(65.1, 47.1) * mm});
            skLineSegment(sketch, "E9.4.0.27", {"start": v(35.08, 51.72) * mm, "end": v(35.08, 47.1) * mm});
            skLineSegment(sketch, "E9.4.0.28", {"start": v(85.88, 51.72) * mm, "end": v(85.88, 47.1) * mm});
            skLineSegment(sketch, "E9.4.0.29", {"start": v(-53.82, 47.1) * mm, "end": v(-49.2, 47.1) * mm});
            skLineSegment(sketch, "E9.4.0.30", {"start": v(-66.52, 51.72) * mm, "end": v(-61.9, 51.72) * mm});
            skLineSegment(sketch, "E9.4.0.31", {"start": v(111.28, 47.1) * mm, "end": v(115.9, 47.1) * mm});
            skLineSegment(sketch, "E9.4.0.32", {"start": v(-74.6, 51.72) * mm, "end": v(-74.6, 47.1) * mm});
            skLineSegment(sketch, "E9.4.0.33", {"start": v(-79.22, 51.72) * mm, "end": v(-79.22, 47.1) * mm});
            skLineSegment(sketch, "E9.4.0.34", {"start": v(-79.22, 51.72) * mm, "end": v(-74.6, 51.72) * mm});
            skLineSegment(sketch, "E9.4.0.35", {"start": v(-41.12, 51.72) * mm, "end": v(-41.12, 47.1) * mm});
            skLineSegment(sketch, "E9.4.0.36", {"start": v(-11.1, 51.72) * mm, "end": v(-11.1, 47.1) * mm});
            skLineSegment(sketch, "E9.4.0.37", {"start": v(-3.02, 47.1) * mm, "end": v(1.6, 47.1) * mm});
            skLineSegment(sketch, "E9.4.0.38", {"start": v(47.78, 47.1) * mm, "end": v(52.4, 47.1) * mm});
            skLineSegment(sketch, "E9.4.0.39", {"start": v(98.58, 47.1) * mm, "end": v(103.2, 47.1) * mm});
            skLineSegment(sketch, "E9.4.0.40", {"start": v(9.68, 51.72) * mm, "end": v(14.3, 51.72) * mm});
            skLineSegment(sketch, "E9.4.0.41", {"start": v(14.3, 51.72) * mm, "end": v(14.3, 47.1) * mm});
            skLineSegment(sketch, "E9.4.0.42", {"start": v(22.38, 47.1) * mm, "end": v(27, 47.1) * mm});
            skLineSegment(sketch, "E9.4.0.43", {"start": v(73.18, 47.1) * mm, "end": v(77.8, 47.1) * mm});
            skLineSegment(sketch, "E9.4.0.44", {"start": v(115.9, 51.72) * mm, "end": v(115.9, 47.1) * mm});
            skLineSegment(sketch, "E9.4.0.45", {"start": v(60.48, 51.72) * mm, "end": v(65.1, 51.72) * mm});
            skLineSegment(sketch, "E9.4.0.46", {"start": v(111.28, 51.72) * mm, "end": v(115.9, 51.72) * mm});
            skLineSegment(sketch, "E9.4.0.47", {"start": v(-15.72, 51.72) * mm, "end": v(-11.1, 51.72) * mm});
            skLineSegment(sketch, "E9.4.0.48", {"start": v(35.08, 51.72) * mm, "end": v(39.7, 51.72) * mm});
            skLineSegment(sketch, "E9.4.0.49", {"start": v(-23.8, 51.72) * mm, "end": v(-23.8, 47.1) * mm});
            skLineSegment(sketch, "E9.4.0.50", {"start": v(85.88, 51.72) * mm, "end": v(90.5, 51.72) * mm});
            skLineSegment(sketch, "E9.4.0.51", {"start": v(65.1, 51.72) * mm, "end": v(65.1, 47.1) * mm});
            skLineSegment(sketch, "E9.4.0.52", {"start": v(52.4, 51.72) * mm, "end": v(52.4, 47.1) * mm});
            skLineSegment(sketch, "E9.4.0.53", {"start": v(103.2, 51.72) * mm, "end": v(103.2, 47.1) * mm});
            skLineSegment(sketch, "E9.4.0.54", {"start": v(-15.72, 47.1) * mm, "end": v(-11.1, 47.1) * mm});
            skLineSegment(sketch, "E9.4.0.55", {"start": v(111.28, 51.72) * mm, "end": v(111.28, 47.1) * mm});
            skLineSegment(sketch, "E9.4.0.56", {"start": v(60.48, 51.72) * mm, "end": v(60.48, 47.1) * mm});
            skLineSegment(sketch, "E9.4.0.57", {"start": v(85.88, 47.1) * mm, "end": v(90.5, 47.1) * mm});
            skLineSegment(sketch, "E9.4.0.58", {"start": v(35.08, 47.1) * mm, "end": v(39.7, 47.1) * mm});
            skLineSegment(sketch, "E9.4.0.59", {"start": v(9.68, 51.72) * mm, "end": v(9.68, 47.1) * mm});
            skLineSegment(sketch, "E9.4.0.60", {"start": v(-36.5, 51.72) * mm, "end": v(-36.5, 47.1) * mm});
            skLineSegment(sketch, "E9.4.0.61", {"start": v(-41.12, 47.1) * mm, "end": v(-36.5, 47.1) * mm});
            skLineSegment(sketch, "E9.4.0.62", {"start": v(-79.22, 47.1) * mm, "end": v(-74.6, 47.1) * mm});
            skLineSegment(sketch, "E9.4.0.63", {"start": v(-66.52, 47.1) * mm, "end": v(-61.9, 47.1) * mm});
            skLineSegment(sketch, "E9.4.0.64", {"start": v(-66.52, 51.72) * mm, "end": v(-66.52, 47.1) * mm});
            skLineSegment(sketch, "E9.4.0.65", {"start": v(-61.9, 51.72) * mm, "end": v(-61.9, 47.1) * mm});
            skLineSegment(sketch, "E9.4.0.66", {"start": v(-53.82, 51.72) * mm, "end": v(-53.82, 47.1) * mm});
            skLineSegment(sketch, "E9.4.0.67", {"start": v(-3.02, 51.72) * mm, "end": v(-3.02, 47.1) * mm});
            skLineSegment(sketch, "E9.4.0.68", {"start": v(22.38, 51.72) * mm, "end": v(22.38, 47.1) * mm});
            skLineSegment(sketch, "E9.4.0.69", {"start": v(-49.2, 51.72) * mm, "end": v(-49.2, 47.1) * mm});
            skLineSegment(sketch, "E9.4.0.70", {"start": v(1.6, 51.72) * mm, "end": v(1.6, 47.1) * mm});
            skLineSegment(sketch, "E9.4.0.71", {"start": v(77.8, 51.72) * mm, "end": v(77.8, 47.1) * mm});
            skLineSegment(sketch, "E9.4.0.72", {"start": v(27, 51.72) * mm, "end": v(27, 47.1) * mm});
            skLineSegment(sketch, "E9.4.0.73", {"start": v(-41.12, 51.72) * mm, "end": v(-36.5, 51.72) * mm});
            skLineSegment(sketch, "E9.4.0.74", {"start": v(-28.42, 47.1) * mm, "end": v(-23.8, 47.1) * mm});
            skLineSegment(sketch, "E9.4.0.75", {"start": v(-28.42, 51.72) * mm, "end": v(-23.8, 51.72) * mm});
            skLineSegment(sketch, "E9.4.0.76", {"start": v(22.38, 51.72) * mm, "end": v(27, 51.72) * mm});
            skLineSegment(sketch, "E9.4.0.77", {"start": v(73.18, 51.72) * mm, "end": v(77.8, 51.72) * mm});
            skLineSegment(sketch, "E9.4.0.78", {"start": v(-3.02, 51.72) * mm, "end": v(1.6, 51.72) * mm});
            skLineSegment(sketch, "E9.4.0.79", {"start": v(47.78, 51.72) * mm, "end": v(52.4, 51.72) * mm});
            skLineSegment(sketch, "E9.4.0.80", {"start": v(98.58, 51.72) * mm, "end": v(103.2, 51.72) * mm});
            skLineSegment(sketch, "E9.4.0.81", {"start": v(-53.82, 51.72) * mm, "end": v(-49.2, 51.72) * mm});
            skPoint(sketch, "E9.5.0.0", {"position": v(-79.2, 36.71) * mm});
            skPoint(sketch, "E9.5.0.1", {"position": v(88.2, 39.02) * mm});
            skPoint(sketch, "E9.5.0.2", {"position": v(37.4, 39.02) * mm});
            skPoint(sketch, "E9.5.0.3", {"position": v(-51.5, 39.02) * mm});
            skPoint(sketch, "E9.5.0.4", {"position": v(113.6, 39.02) * mm});
            skPoint(sketch, "E9.5.0.5", {"position": v(-64.2, 39.02) * mm});
            skPoint(sketch, "E9.5.0.6", {"position": v(24.7, 39.02) * mm});
            skPoint(sketch, "E9.5.0.7", {"position": v(12, 39.02) * mm});
            skLineSegment(sketch, "E9.5.0.8", {"start": v(-76.9, 39.02) * mm, "end": v(-51.5, 39.02) * mm, "construction": true});
            skPoint(sketch, "E9.5.0.9", {"position": v(-76.9, 39.02) * mm});
            skPoint(sketch, "E9.5.0.10", {"position": v(-13.4, 39.02) * mm});
            skPoint(sketch, "E9.5.0.11", {"position": v(50.1, 39.02) * mm});
            skPoint(sketch, "E9.5.0.12", {"position": v(-38.8, 39.02) * mm});
            skPoint(sketch, "E9.5.0.13", {"position": v(62.8, 39.02) * mm});
            skPoint(sketch, "E9.5.0.14", {"position": v(-26.1, 39.02) * mm});
            skPoint(sketch, "E9.5.0.15", {"position": v(75.5, 39.02) * mm});
            skPoint(sketch, "E9.5.0.16", {"position": v(-0.7, 39.02) * mm});
            skPoint(sketch, "E9.5.0.17", {"position": v(100.9, 39.02) * mm});
            skLineSegment(sketch, "E9.5.0.18", {"start": v(90.52, 39.02) * mm, "end": v(90.52, 34.4) * mm});
            skLineSegment(sketch, "E9.5.0.19", {"start": v(47.8, 39.02) * mm, "end": v(47.8, 34.4) * mm});
            skLineSegment(sketch, "E9.5.0.20", {"start": v(-28.4, 39.02) * mm, "end": v(-28.4, 34.4) * mm});
            skLineSegment(sketch, "E9.5.0.21", {"start": v(73.2, 39.02) * mm, "end": v(73.2, 34.4) * mm});
            skLineSegment(sketch, "E9.5.0.22", {"start": v(9.7, 34.4) * mm, "end": v(14.32, 34.4) * mm});
            skLineSegment(sketch, "E9.5.0.23", {"start": v(98.6, 39.02) * mm, "end": v(98.6, 34.4) * mm});
            skLineSegment(sketch, "E9.5.0.24", {"start": v(39.72, 39.02) * mm, "end": v(39.72, 34.4) * mm});
            skLineSegment(sketch, "E9.5.0.25", {"start": v(-15.7, 39.02) * mm, "end": v(-15.7, 34.4) * mm});
            skLineSegment(sketch, "E9.5.0.26", {"start": v(60.5, 34.4) * mm, "end": v(65.12, 34.4) * mm});
            skLineSegment(sketch, "E9.5.0.27", {"start": v(35.1, 39.02) * mm, "end": v(35.1, 34.4) * mm});
            skLineSegment(sketch, "E9.5.0.28", {"start": v(85.9, 39.02) * mm, "end": v(85.9, 34.4) * mm});
            skLineSegment(sketch, "E9.5.0.29", {"start": v(-53.8, 34.4) * mm, "end": v(-49.18, 34.4) * mm});
            skLineSegment(sketch, "E9.5.0.30", {"start": v(-66.5, 39.02) * mm, "end": v(-61.88, 39.02) * mm});
            skLineSegment(sketch, "E9.5.0.31", {"start": v(111.3, 34.4) * mm, "end": v(115.92, 34.4) * mm});
            skLineSegment(sketch, "E9.5.0.32", {"start": v(-74.58, 39.02) * mm, "end": v(-74.58, 34.4) * mm});
            skLineSegment(sketch, "E9.5.0.33", {"start": v(-79.2, 39.02) * mm, "end": v(-79.2, 34.4) * mm});
            skLineSegment(sketch, "E9.5.0.34", {"start": v(-79.2, 39.02) * mm, "end": v(-74.58, 39.02) * mm});
            skLineSegment(sketch, "E9.5.0.35", {"start": v(-41.1, 39.02) * mm, "end": v(-41.1, 34.4) * mm});
            skLineSegment(sketch, "E9.5.0.36", {"start": v(-11.08, 39.02) * mm, "end": v(-11.08, 34.4) * mm});
            skLineSegment(sketch, "E9.5.0.37", {"start": v(-3, 34.4) * mm, "end": v(1.62, 34.4) * mm});
            skLineSegment(sketch, "E9.5.0.38", {"start": v(47.8, 34.4) * mm, "end": v(52.42, 34.4) * mm});
            skLineSegment(sketch, "E9.5.0.39", {"start": v(98.6, 34.4) * mm, "end": v(103.22, 34.4) * mm});
            skLineSegment(sketch, "E9.5.0.40", {"start": v(9.7, 39.02) * mm, "end": v(14.32, 39.02) * mm});
            skLineSegment(sketch, "E9.5.0.41", {"start": v(14.32, 39.02) * mm, "end": v(14.32, 34.4) * mm});
            skLineSegment(sketch, "E9.5.0.42", {"start": v(22.4, 34.4) * mm, "end": v(27.02, 34.4) * mm});
            skLineSegment(sketch, "E9.5.0.43", {"start": v(73.2, 34.4) * mm, "end": v(77.82, 34.4) * mm});
            skLineSegment(sketch, "E9.5.0.44", {"start": v(115.92, 39.02) * mm, "end": v(115.92, 34.4) * mm});
            skLineSegment(sketch, "E9.5.0.45", {"start": v(60.5, 39.02) * mm, "end": v(65.12, 39.02) * mm});
            skLineSegment(sketch, "E9.5.0.46", {"start": v(111.3, 39.02) * mm, "end": v(115.92, 39.02) * mm});
            skLineSegment(sketch, "E9.5.0.47", {"start": v(-15.7, 39.02) * mm, "end": v(-11.08, 39.02) * mm});
            skLineSegment(sketch, "E9.5.0.48", {"start": v(35.1, 39.02) * mm, "end": v(39.72, 39.02) * mm});
            skLineSegment(sketch, "E9.5.0.49", {"start": v(-23.78, 39.02) * mm, "end": v(-23.78, 34.4) * mm});
            skLineSegment(sketch, "E9.5.0.50", {"start": v(85.9, 39.02) * mm, "end": v(90.52, 39.02) * mm});
            skLineSegment(sketch, "E9.5.0.51", {"start": v(65.12, 39.02) * mm, "end": v(65.12, 34.4) * mm});
            skLineSegment(sketch, "E9.5.0.52", {"start": v(52.42, 39.02) * mm, "end": v(52.42, 34.4) * mm});
            skLineSegment(sketch, "E9.5.0.53", {"start": v(103.22, 39.02) * mm, "end": v(103.22, 34.4) * mm});
            skLineSegment(sketch, "E9.5.0.54", {"start": v(-15.7, 34.4) * mm, "end": v(-11.08, 34.4) * mm});
            skLineSegment(sketch, "E9.5.0.55", {"start": v(111.3, 39.02) * mm, "end": v(111.3, 34.4) * mm});
            skLineSegment(sketch, "E9.5.0.56", {"start": v(60.5, 39.02) * mm, "end": v(60.5, 34.4) * mm});
            skLineSegment(sketch, "E9.5.0.57", {"start": v(85.9, 34.4) * mm, "end": v(90.52, 34.4) * mm});
            skLineSegment(sketch, "E9.5.0.58", {"start": v(35.1, 34.4) * mm, "end": v(39.72, 34.4) * mm});
            skLineSegment(sketch, "E9.5.0.59", {"start": v(9.7, 39.02) * mm, "end": v(9.7, 34.4) * mm});
            skLineSegment(sketch, "E9.5.0.60", {"start": v(-36.48, 39.02) * mm, "end": v(-36.48, 34.4) * mm});
            skLineSegment(sketch, "E9.5.0.61", {"start": v(-41.1, 34.4) * mm, "end": v(-36.48, 34.4) * mm});
            skLineSegment(sketch, "E9.5.0.62", {"start": v(-79.2, 34.4) * mm, "end": v(-74.58, 34.4) * mm});
            skLineSegment(sketch, "E9.5.0.63", {"start": v(-66.5, 34.4) * mm, "end": v(-61.88, 34.4) * mm});
            skLineSegment(sketch, "E9.5.0.64", {"start": v(-66.5, 39.02) * mm, "end": v(-66.5, 34.4) * mm});
            skLineSegment(sketch, "E9.5.0.65", {"start": v(-61.88, 39.02) * mm, "end": v(-61.88, 34.4) * mm});
            skLineSegment(sketch, "E9.5.0.66", {"start": v(-53.8, 39.02) * mm, "end": v(-53.8, 34.4) * mm});
            skLineSegment(sketch, "E9.5.0.67", {"start": v(-3, 39.02) * mm, "end": v(-3, 34.4) * mm});
            skLineSegment(sketch, "E9.5.0.68", {"start": v(22.4, 39.02) * mm, "end": v(22.4, 34.4) * mm});
            skLineSegment(sketch, "E9.5.0.69", {"start": v(-49.18, 39.02) * mm, "end": v(-49.18, 34.4) * mm});
            skLineSegment(sketch, "E9.5.0.70", {"start": v(1.62, 39.02) * mm, "end": v(1.62, 34.4) * mm});
            skLineSegment(sketch, "E9.5.0.71", {"start": v(77.82, 39.02) * mm, "end": v(77.82, 34.4) * mm});
            skLineSegment(sketch, "E9.5.0.72", {"start": v(27.02, 39.02) * mm, "end": v(27.02, 34.4) * mm});
            skLineSegment(sketch, "E9.5.0.73", {"start": v(-41.1, 39.02) * mm, "end": v(-36.48, 39.02) * mm});
            skLineSegment(sketch, "E9.5.0.74", {"start": v(-28.4, 34.4) * mm, "end": v(-23.78, 34.4) * mm});
            skLineSegment(sketch, "E9.5.0.75", {"start": v(-28.4, 39.02) * mm, "end": v(-23.78, 39.02) * mm});
            skLineSegment(sketch, "E9.5.0.76", {"start": v(22.4, 39.02) * mm, "end": v(27.02, 39.02) * mm});
            skLineSegment(sketch, "E9.5.0.77", {"start": v(73.2, 39.02) * mm, "end": v(77.82, 39.02) * mm});
            skLineSegment(sketch, "E9.5.0.78", {"start": v(-3, 39.02) * mm, "end": v(1.62, 39.02) * mm});
            skLineSegment(sketch, "E9.5.0.79", {"start": v(47.8, 39.02) * mm, "end": v(52.42, 39.02) * mm});
            skLineSegment(sketch, "E9.5.0.80", {"start": v(98.6, 39.02) * mm, "end": v(103.22, 39.02) * mm});
            skLineSegment(sketch, "E9.5.0.81", {"start": v(-53.8, 39.02) * mm, "end": v(-49.18, 39.02) * mm});
            skPoint(sketch, "E9.6.0.0", {"position": v(-79.2, 24.01) * mm});
            skPoint(sketch, "E9.6.0.1", {"position": v(88.22, 26.32) * mm});
            skPoint(sketch, "E9.6.0.2", {"position": v(37.42, 26.32) * mm});
            skPoint(sketch, "E9.6.0.3", {"position": v(-51.48, 26.32) * mm});
            skPoint(sketch, "E9.6.0.4", {"position": v(113.62, 26.32) * mm});
            skPoint(sketch, "E9.6.0.5", {"position": v(-64.18, 26.32) * mm});
            skPoint(sketch, "E9.6.0.6", {"position": v(24.72, 26.32) * mm});
            skPoint(sketch, "E9.6.0.7", {"position": v(12.02, 26.32) * mm});
            skLineSegment(sketch, "E9.6.0.8", {"start": v(-76.88, 26.32) * mm, "end": v(-51.48, 26.32) * mm, "construction": true});
            skPoint(sketch, "E9.6.0.9", {"position": v(-76.88, 26.32) * mm});
            skPoint(sketch, "E9.6.0.10", {"position": v(-13.38, 26.32) * mm});
            skPoint(sketch, "E9.6.0.11", {"position": v(50.12, 26.32) * mm});
            skPoint(sketch, "E9.6.0.12", {"position": v(-38.78, 26.32) * mm});
            skPoint(sketch, "E9.6.0.13", {"position": v(62.82, 26.32) * mm});
            skPoint(sketch, "E9.6.0.14", {"position": v(-26.08, 26.32) * mm});
            skPoint(sketch, "E9.6.0.15", {"position": v(75.52, 26.32) * mm});
            skPoint(sketch, "E9.6.0.16", {"position": v(-0.68, 26.32) * mm});
            skPoint(sketch, "E9.6.0.17", {"position": v(100.92, 26.32) * mm});
            skLineSegment(sketch, "E9.6.0.18", {"start": v(90.53, 26.32) * mm, "end": v(90.53, 21.7) * mm});
            skLineSegment(sketch, "E9.6.0.19", {"start": v(47.8, 26.32) * mm, "end": v(47.8, 21.7) * mm});
            skLineSegment(sketch, "E9.6.0.20", {"start": v(-28.4, 26.32) * mm, "end": v(-28.4, 21.7) * mm});
            skLineSegment(sketch, "E9.6.0.21", {"start": v(73.2, 26.32) * mm, "end": v(73.2, 21.7) * mm});
            skLineSegment(sketch, "E9.6.0.22", {"start": v(9.7, 21.7) * mm, "end": v(14.33, 21.7) * mm});
            skLineSegment(sketch, "E9.6.0.23", {"start": v(98.6, 26.32) * mm, "end": v(98.6, 21.7) * mm});
            skLineSegment(sketch, "E9.6.0.24", {"start": v(39.73, 26.32) * mm, "end": v(39.73, 21.7) * mm});
            skLineSegment(sketch, "E9.6.0.25", {"start": v(-15.7, 26.32) * mm, "end": v(-15.7, 21.7) * mm});
            skLineSegment(sketch, "E9.6.0.26", {"start": v(60.5, 21.7) * mm, "end": v(65.13, 21.7) * mm});
            skLineSegment(sketch, "E9.6.0.27", {"start": v(35.1, 26.32) * mm, "end": v(35.1, 21.7) * mm});
            skLineSegment(sketch, "E9.6.0.28", {"start": v(85.9, 26.32) * mm, "end": v(85.9, 21.7) * mm});
            skLineSegment(sketch, "E9.6.0.29", {"start": v(-53.8, 21.7) * mm, "end": v(-49.17, 21.7) * mm});
            skLineSegment(sketch, "E9.6.0.30", {"start": v(-66.5, 26.32) * mm, "end": v(-61.87, 26.32) * mm});
            skLineSegment(sketch, "E9.6.0.31", {"start": v(111.3, 21.7) * mm, "end": v(115.93, 21.7) * mm});
            skLineSegment(sketch, "E9.6.0.32", {"start": v(-74.57, 26.32) * mm, "end": v(-74.57, 21.7) * mm});
            skLineSegment(sketch, "E9.6.0.33", {"start": v(-79.2, 26.32) * mm, "end": v(-79.2, 21.7) * mm});
            skLineSegment(sketch, "E9.6.0.34", {"start": v(-79.2, 26.32) * mm, "end": v(-74.57, 26.32) * mm});
            skLineSegment(sketch, "E9.6.0.35", {"start": v(-41.1, 26.32) * mm, "end": v(-41.1, 21.7) * mm});
            skLineSegment(sketch, "E9.6.0.36", {"start": v(-11.07, 26.32) * mm, "end": v(-11.07, 21.7) * mm});
            skLineSegment(sketch, "E9.6.0.37", {"start": v(-3, 21.7) * mm, "end": v(1.63, 21.7) * mm});
            skLineSegment(sketch, "E9.6.0.38", {"start": v(47.8, 21.7) * mm, "end": v(52.43, 21.7) * mm});
            skLineSegment(sketch, "E9.6.0.39", {"start": v(98.6, 21.7) * mm, "end": v(103.23, 21.7) * mm});
            skLineSegment(sketch, "E9.6.0.40", {"start": v(9.7, 26.32) * mm, "end": v(14.33, 26.32) * mm});
            skLineSegment(sketch, "E9.6.0.41", {"start": v(14.33, 26.32) * mm, "end": v(14.33, 21.7) * mm});
            skLineSegment(sketch, "E9.6.0.42", {"start": v(22.4, 21.7) * mm, "end": v(27.03, 21.7) * mm});
            skLineSegment(sketch, "E9.6.0.43", {"start": v(73.2, 21.7) * mm, "end": v(77.83, 21.7) * mm});
            skLineSegment(sketch, "E9.6.0.44", {"start": v(115.93, 26.32) * mm, "end": v(115.93, 21.7) * mm});
            skLineSegment(sketch, "E9.6.0.45", {"start": v(60.5, 26.32) * mm, "end": v(65.13, 26.32) * mm});
            skLineSegment(sketch, "E9.6.0.46", {"start": v(111.3, 26.32) * mm, "end": v(115.93, 26.32) * mm});
            skLineSegment(sketch, "E9.6.0.47", {"start": v(-15.7, 26.32) * mm, "end": v(-11.07, 26.32) * mm});
            skLineSegment(sketch, "E9.6.0.48", {"start": v(35.1, 26.32) * mm, "end": v(39.73, 26.32) * mm});
            skLineSegment(sketch, "E9.6.0.49", {"start": v(-23.77, 26.32) * mm, "end": v(-23.77, 21.7) * mm});
            skLineSegment(sketch, "E9.6.0.50", {"start": v(85.9, 26.32) * mm, "end": v(90.53, 26.32) * mm});
            skLineSegment(sketch, "E9.6.0.51", {"start": v(65.13, 26.32) * mm, "end": v(65.13, 21.7) * mm});
            skLineSegment(sketch, "E9.6.0.52", {"start": v(52.43, 26.32) * mm, "end": v(52.43, 21.7) * mm});
            skLineSegment(sketch, "E9.6.0.53", {"start": v(103.23, 26.32) * mm, "end": v(103.23, 21.7) * mm});
            skLineSegment(sketch, "E9.6.0.54", {"start": v(-15.7, 21.7) * mm, "end": v(-11.07, 21.7) * mm});
            skLineSegment(sketch, "E9.6.0.55", {"start": v(111.3, 26.32) * mm, "end": v(111.3, 21.7) * mm});
            skLineSegment(sketch, "E9.6.0.56", {"start": v(60.5, 26.32) * mm, "end": v(60.5, 21.7) * mm});
            skLineSegment(sketch, "E9.6.0.57", {"start": v(85.9, 21.7) * mm, "end": v(90.53, 21.7) * mm});
            skLineSegment(sketch, "E9.6.0.58", {"start": v(35.1, 21.7) * mm, "end": v(39.73, 21.7) * mm});
            skLineSegment(sketch, "E9.6.0.59", {"start": v(9.7, 26.32) * mm, "end": v(9.7, 21.7) * mm});
            skLineSegment(sketch, "E9.6.0.60", {"start": v(-36.47, 26.32) * mm, "end": v(-36.47, 21.7) * mm});
            skLineSegment(sketch, "E9.6.0.61", {"start": v(-41.1, 21.7) * mm, "end": v(-36.47, 21.7) * mm});
            skLineSegment(sketch, "E9.6.0.62", {"start": v(-79.2, 21.7) * mm, "end": v(-74.57, 21.7) * mm});
            skLineSegment(sketch, "E9.6.0.63", {"start": v(-66.5, 21.7) * mm, "end": v(-61.87, 21.7) * mm});
            skLineSegment(sketch, "E9.6.0.64", {"start": v(-66.5, 26.32) * mm, "end": v(-66.5, 21.7) * mm});
            skLineSegment(sketch, "E9.6.0.65", {"start": v(-61.87, 26.32) * mm, "end": v(-61.87, 21.7) * mm});
            skLineSegment(sketch, "E9.6.0.66", {"start": v(-53.8, 26.32) * mm, "end": v(-53.8, 21.7) * mm});
            skLineSegment(sketch, "E9.6.0.67", {"start": v(-3, 26.32) * mm, "end": v(-3, 21.7) * mm});
            skLineSegment(sketch, "E9.6.0.68", {"start": v(22.4, 26.32) * mm, "end": v(22.4, 21.7) * mm});
            skLineSegment(sketch, "E9.6.0.69", {"start": v(-49.17, 26.32) * mm, "end": v(-49.17, 21.7) * mm});
            skLineSegment(sketch, "E9.6.0.70", {"start": v(1.63, 26.32) * mm, "end": v(1.63, 21.7) * mm});
            skLineSegment(sketch, "E9.6.0.71", {"start": v(77.83, 26.32) * mm, "end": v(77.83, 21.7) * mm});
            skLineSegment(sketch, "E9.6.0.72", {"start": v(27.03, 26.32) * mm, "end": v(27.03, 21.7) * mm});
            skLineSegment(sketch, "E9.6.0.73", {"start": v(-41.1, 26.32) * mm, "end": v(-36.47, 26.32) * mm});
            skLineSegment(sketch, "E9.6.0.74", {"start": v(-28.4, 21.7) * mm, "end": v(-23.77, 21.7) * mm});
            skLineSegment(sketch, "E9.6.0.75", {"start": v(-28.4, 26.32) * mm, "end": v(-23.77, 26.32) * mm});
            skLineSegment(sketch, "E9.6.0.76", {"start": v(22.4, 26.32) * mm, "end": v(27.03, 26.32) * mm});
            skLineSegment(sketch, "E9.6.0.77", {"start": v(73.2, 26.32) * mm, "end": v(77.83, 26.32) * mm});
            skLineSegment(sketch, "E9.6.0.78", {"start": v(-3, 26.32) * mm, "end": v(1.63, 26.32) * mm});
            skLineSegment(sketch, "E9.6.0.79", {"start": v(47.8, 26.32) * mm, "end": v(52.43, 26.32) * mm});
            skLineSegment(sketch, "E9.6.0.80", {"start": v(98.6, 26.32) * mm, "end": v(103.23, 26.32) * mm});
            skLineSegment(sketch, "E9.6.0.81", {"start": v(-53.8, 26.32) * mm, "end": v(-49.17, 26.32) * mm});
            skPoint(sketch, "E9.7.0.0", {"position": v(-79.18, 11.31) * mm});
            skPoint(sketch, "E9.7.0.1", {"position": v(88.23, 13.62) * mm});
            skPoint(sketch, "E9.7.0.2", {"position": v(37.43, 13.62) * mm});
            skPoint(sketch, "E9.7.0.3", {"position": v(-51.47, 13.62) * mm});
            skPoint(sketch, "E9.7.0.4", {"position": v(113.63, 13.62) * mm});
            skPoint(sketch, "E9.7.0.5", {"position": v(-64.17, 13.62) * mm});
            skPoint(sketch, "E9.7.0.6", {"position": v(24.73, 13.62) * mm});
            skPoint(sketch, "E9.7.0.7", {"position": v(12.03, 13.62) * mm});
            skLineSegment(sketch, "E9.7.0.8", {"start": v(-76.87, 13.62) * mm, "end": v(-51.47, 13.62) * mm, "construction": true});
            skPoint(sketch, "E9.7.0.9", {"position": v(-76.87, 13.62) * mm});
            skPoint(sketch, "E9.7.0.10", {"position": v(-13.37, 13.62) * mm});
            skPoint(sketch, "E9.7.0.11", {"position": v(50.13, 13.62) * mm});
            skPoint(sketch, "E9.7.0.12", {"position": v(-38.77, 13.62) * mm});
            skPoint(sketch, "E9.7.0.13", {"position": v(62.83, 13.62) * mm});
            skPoint(sketch, "E9.7.0.14", {"position": v(-26.07, 13.62) * mm});
            skPoint(sketch, "E9.7.0.15", {"position": v(75.53, 13.62) * mm});
            skPoint(sketch, "E9.7.0.16", {"position": v(-0.67, 13.62) * mm});
            skPoint(sketch, "E9.7.0.17", {"position": v(100.93, 13.62) * mm});
            skLineSegment(sketch, "E9.7.0.18", {"start": v(90.54, 13.62) * mm, "end": v(90.54, 9) * mm});
            skLineSegment(sketch, "E9.7.0.19", {"start": v(47.82, 13.62) * mm, "end": v(47.82, 9) * mm});
            skLineSegment(sketch, "E9.7.0.20", {"start": v(-28.38, 13.62) * mm, "end": v(-28.38, 9) * mm});
            skLineSegment(sketch, "E9.7.0.21", {"start": v(73.22, 13.62) * mm, "end": v(73.22, 9) * mm});
            skLineSegment(sketch, "E9.7.0.22", {"start": v(9.72, 9) * mm, "end": v(14.34, 9) * mm});
            skLineSegment(sketch, "E9.7.0.23", {"start": v(98.62, 13.62) * mm, "end": v(98.62, 9) * mm});
            skLineSegment(sketch, "E9.7.0.24", {"start": v(39.74, 13.62) * mm, "end": v(39.74, 9) * mm});
            skLineSegment(sketch, "E9.7.0.25", {"start": v(-15.68, 13.62) * mm, "end": v(-15.68, 9) * mm});
            skLineSegment(sketch, "E9.7.0.26", {"start": v(60.52, 9) * mm, "end": v(65.14, 9) * mm});
            skLineSegment(sketch, "E9.7.0.27", {"start": v(35.12, 13.62) * mm, "end": v(35.12, 9) * mm});
            skLineSegment(sketch, "E9.7.0.28", {"start": v(85.92, 13.62) * mm, "end": v(85.92, 9) * mm});
            skLineSegment(sketch, "E9.7.0.29", {"start": v(-53.78, 9) * mm, "end": v(-49.16, 9) * mm});
            skLineSegment(sketch, "E9.7.0.30", {"start": v(-66.48, 13.62) * mm, "end": v(-61.86, 13.62) * mm});
            skLineSegment(sketch, "E9.7.0.31", {"start": v(111.32, 9) * mm, "end": v(115.94, 9) * mm});
            skLineSegment(sketch, "E9.7.0.32", {"start": v(-74.56, 13.62) * mm, "end": v(-74.56, 9) * mm});
            skLineSegment(sketch, "E9.7.0.33", {"start": v(-79.18, 13.62) * mm, "end": v(-79.18, 9) * mm});
            skLineSegment(sketch, "E9.7.0.34", {"start": v(-79.18, 13.62) * mm, "end": v(-74.56, 13.62) * mm});
            skLineSegment(sketch, "E9.7.0.35", {"start": v(-41.08, 13.62) * mm, "end": v(-41.08, 9) * mm});
            skLineSegment(sketch, "E9.7.0.36", {"start": v(-11.06, 13.62) * mm, "end": v(-11.06, 9) * mm});
            skLineSegment(sketch, "E9.7.0.37", {"start": v(-2.98, 9) * mm, "end": v(1.64, 9) * mm});
            skLineSegment(sketch, "E9.7.0.38", {"start": v(47.82, 9) * mm, "end": v(52.44, 9) * mm});
            skLineSegment(sketch, "E9.7.0.39", {"start": v(98.62, 9) * mm, "end": v(103.24, 9) * mm});
            skLineSegment(sketch, "E9.7.0.40", {"start": v(9.72, 13.62) * mm, "end": v(14.34, 13.62) * mm});
            skLineSegment(sketch, "E9.7.0.41", {"start": v(14.34, 13.62) * mm, "end": v(14.34, 9) * mm});
            skLineSegment(sketch, "E9.7.0.42", {"start": v(22.42, 9) * mm, "end": v(27.04, 9) * mm});
            skLineSegment(sketch, "E9.7.0.43", {"start": v(73.22, 9) * mm, "end": v(77.84, 9) * mm});
            skLineSegment(sketch, "E9.7.0.44", {"start": v(115.94, 13.62) * mm, "end": v(115.94, 9) * mm});
            skLineSegment(sketch, "E9.7.0.45", {"start": v(60.52, 13.62) * mm, "end": v(65.14, 13.62) * mm});
            skLineSegment(sketch, "E9.7.0.46", {"start": v(111.32, 13.62) * mm, "end": v(115.94, 13.62) * mm});
            skLineSegment(sketch, "E9.7.0.47", {"start": v(-15.68, 13.62) * mm, "end": v(-11.06, 13.62) * mm});
            skLineSegment(sketch, "E9.7.0.48", {"start": v(35.12, 13.62) * mm, "end": v(39.74, 13.62) * mm});
            skLineSegment(sketch, "E9.7.0.49", {"start": v(-23.76, 13.62) * mm, "end": v(-23.76, 9) * mm});
            skLineSegment(sketch, "E9.7.0.50", {"start": v(85.92, 13.62) * mm, "end": v(90.54, 13.62) * mm});
            skLineSegment(sketch, "E9.7.0.51", {"start": v(65.14, 13.62) * mm, "end": v(65.14, 9) * mm});
            skLineSegment(sketch, "E9.7.0.52", {"start": v(52.44, 13.62) * mm, "end": v(52.44, 9) * mm});
            skLineSegment(sketch, "E9.7.0.53", {"start": v(103.24, 13.62) * mm, "end": v(103.24, 9) * mm});
            skLineSegment(sketch, "E9.7.0.54", {"start": v(-15.68, 9) * mm, "end": v(-11.06, 9) * mm});
            skLineSegment(sketch, "E9.7.0.55", {"start": v(111.32, 13.62) * mm, "end": v(111.32, 9) * mm});
            skLineSegment(sketch, "E9.7.0.56", {"start": v(60.52, 13.62) * mm, "end": v(60.52, 9) * mm});
            skLineSegment(sketch, "E9.7.0.57", {"start": v(85.92, 9) * mm, "end": v(90.54, 9) * mm});
            skLineSegment(sketch, "E9.7.0.58", {"start": v(35.12, 9) * mm, "end": v(39.74, 9) * mm});
            skLineSegment(sketch, "E9.7.0.59", {"start": v(9.72, 13.62) * mm, "end": v(9.72, 9) * mm});
            skLineSegment(sketch, "E9.7.0.60", {"start": v(-36.46, 13.62) * mm, "end": v(-36.46, 9) * mm});
            skLineSegment(sketch, "E9.7.0.61", {"start": v(-41.08, 9) * mm, "end": v(-36.46, 9) * mm});
            skLineSegment(sketch, "E9.7.0.62", {"start": v(-79.18, 9) * mm, "end": v(-74.56, 9) * mm});
            skLineSegment(sketch, "E9.7.0.63", {"start": v(-66.48, 9) * mm, "end": v(-61.86, 9) * mm});
            skLineSegment(sketch, "E9.7.0.64", {"start": v(-66.48, 13.62) * mm, "end": v(-66.48, 9) * mm});
            skLineSegment(sketch, "E9.7.0.65", {"start": v(-61.86, 13.62) * mm, "end": v(-61.86, 9) * mm});
            skLineSegment(sketch, "E9.7.0.66", {"start": v(-53.78, 13.62) * mm, "end": v(-53.78, 9) * mm});
            skLineSegment(sketch, "E9.7.0.67", {"start": v(-2.98, 13.62) * mm, "end": v(-2.98, 9) * mm});
            skLineSegment(sketch, "E9.7.0.68", {"start": v(22.42, 13.62) * mm, "end": v(22.42, 9) * mm});
            skLineSegment(sketch, "E9.7.0.69", {"start": v(-49.16, 13.62) * mm, "end": v(-49.16, 9) * mm});
            skLineSegment(sketch, "E9.7.0.70", {"start": v(1.64, 13.62) * mm, "end": v(1.64, 9) * mm});
            skLineSegment(sketch, "E9.7.0.71", {"start": v(77.84, 13.62) * mm, "end": v(77.84, 9) * mm});
            skLineSegment(sketch, "E9.7.0.72", {"start": v(27.04, 13.62) * mm, "end": v(27.04, 9) * mm});
            skLineSegment(sketch, "E9.7.0.73", {"start": v(-41.08, 13.62) * mm, "end": v(-36.46, 13.62) * mm});
            skLineSegment(sketch, "E9.7.0.74", {"start": v(-28.38, 9) * mm, "end": v(-23.76, 9) * mm});
            skLineSegment(sketch, "E9.7.0.75", {"start": v(-28.38, 13.62) * mm, "end": v(-23.76, 13.62) * mm});
            skLineSegment(sketch, "E9.7.0.76", {"start": v(22.42, 13.62) * mm, "end": v(27.04, 13.62) * mm});
            skLineSegment(sketch, "E9.7.0.77", {"start": v(73.22, 13.62) * mm, "end": v(77.84, 13.62) * mm});
            skLineSegment(sketch, "E9.7.0.78", {"start": v(-2.98, 13.62) * mm, "end": v(1.64, 13.62) * mm});
            skLineSegment(sketch, "E9.7.0.79", {"start": v(47.82, 13.62) * mm, "end": v(52.44, 13.62) * mm});
            skLineSegment(sketch, "E9.7.0.80", {"start": v(98.62, 13.62) * mm, "end": v(103.24, 13.62) * mm});
            skLineSegment(sketch, "E9.7.0.81", {"start": v(-53.78, 13.62) * mm, "end": v(-49.16, 13.62) * mm});
            skPoint(sketch, "E9.8.0.0", {"position": v(-79.17, -1.39) * mm});
            skPoint(sketch, "E9.8.0.1", {"position": v(88.25, 0.92) * mm});
            skPoint(sketch, "E9.8.0.2", {"position": v(37.45, 0.92) * mm});
            skPoint(sketch, "E9.8.0.3", {"position": v(-51.45, 0.92) * mm});
            skPoint(sketch, "E9.8.0.4", {"position": v(113.65, 0.92) * mm});
            skPoint(sketch, "E9.8.0.5", {"position": v(-64.15, 0.92) * mm});
            skPoint(sketch, "E9.8.0.6", {"position": v(24.75, 0.92) * mm});
            skPoint(sketch, "E9.8.0.7", {"position": v(12.05, 0.92) * mm});
            skLineSegment(sketch, "E9.8.0.8", {"start": v(-76.85, 0.92) * mm, "end": v(-51.45, 0.92) * mm, "construction": true});
            skPoint(sketch, "E9.8.0.9", {"position": v(-76.85, 0.92) * mm});
            skPoint(sketch, "E9.8.0.10", {"position": v(-13.35, 0.92) * mm});
            skPoint(sketch, "E9.8.0.11", {"position": v(50.15, 0.92) * mm});
            skPoint(sketch, "E9.8.0.12", {"position": v(-38.75, 0.92) * mm});
            skPoint(sketch, "E9.8.0.13", {"position": v(62.85, 0.92) * mm});
            skPoint(sketch, "E9.8.0.14", {"position": v(-26.05, 0.92) * mm});
            skPoint(sketch, "E9.8.0.15", {"position": v(75.55, 0.92) * mm});
            skPoint(sketch, "E9.8.0.16", {"position": v(-0.65, 0.92) * mm});
            skPoint(sketch, "E9.8.0.17", {"position": v(100.95, 0.92) * mm});
            skLineSegment(sketch, "E9.8.0.18", {"start": v(90.56, 0.92) * mm, "end": v(90.56, -3.7) * mm});
            skLineSegment(sketch, "E9.8.0.19", {"start": v(47.83, 0.92) * mm, "end": v(47.83, -3.7) * mm});
            skLineSegment(sketch, "E9.8.0.20", {"start": v(-28.37, 0.92) * mm, "end": v(-28.37, -3.7) * mm});
            skLineSegment(sketch, "E9.8.0.21", {"start": v(73.23, 0.92) * mm, "end": v(73.23, -3.7) * mm});
            skLineSegment(sketch, "E9.8.0.22", {"start": v(9.73, -3.7) * mm, "end": v(14.36, -3.7) * mm});
            skLineSegment(sketch, "E9.8.0.23", {"start": v(98.63, 0.92) * mm, "end": v(98.63, -3.7) * mm});
            skLineSegment(sketch, "E9.8.0.24", {"start": v(39.76, 0.92) * mm, "end": v(39.76, -3.7) * mm});
            skLineSegment(sketch, "E9.8.0.25", {"start": v(-15.67, 0.92) * mm, "end": v(-15.67, -3.7) * mm});
            skLineSegment(sketch, "E9.8.0.26", {"start": v(60.53, -3.7) * mm, "end": v(65.16, -3.7) * mm});
            skLineSegment(sketch, "E9.8.0.27", {"start": v(35.13, 0.92) * mm, "end": v(35.13, -3.7) * mm});
            skLineSegment(sketch, "E9.8.0.28", {"start": v(85.93, 0.92) * mm, "end": v(85.93, -3.7) * mm});
            skLineSegment(sketch, "E9.8.0.29", {"start": v(-53.77, -3.7) * mm, "end": v(-49.14, -3.7) * mm});
            skLineSegment(sketch, "E9.8.0.30", {"start": v(-66.47, 0.92) * mm, "end": v(-61.84, 0.92) * mm});
            skLineSegment(sketch, "E9.8.0.31", {"start": v(111.33, -3.7) * mm, "end": v(115.96, -3.7) * mm});
            skLineSegment(sketch, "E9.8.0.32", {"start": v(-74.54, 0.92) * mm, "end": v(-74.54, -3.7) * mm});
            skLineSegment(sketch, "E9.8.0.33", {"start": v(-79.17, 0.92) * mm, "end": v(-79.17, -3.7) * mm});
            skLineSegment(sketch, "E9.8.0.34", {"start": v(-79.17, 0.92) * mm, "end": v(-74.54, 0.92) * mm});
            skLineSegment(sketch, "E9.8.0.35", {"start": v(-41.07, 0.92) * mm, "end": v(-41.07, -3.7) * mm});
            skLineSegment(sketch, "E9.8.0.36", {"start": v(-11.04, 0.92) * mm, "end": v(-11.04, -3.7) * mm});
            skLineSegment(sketch, "E9.8.0.37", {"start": v(-2.97, -3.7) * mm, "end": v(1.66, -3.7) * mm});
            skLineSegment(sketch, "E9.8.0.38", {"start": v(47.83, -3.7) * mm, "end": v(52.46, -3.7) * mm});
            skLineSegment(sketch, "E9.8.0.39", {"start": v(98.63, -3.7) * mm, "end": v(103.26, -3.7) * mm});
            skLineSegment(sketch, "E9.8.0.40", {"start": v(9.73, 0.92) * mm, "end": v(14.36, 0.92) * mm});
            skLineSegment(sketch, "E9.8.0.41", {"start": v(14.36, 0.92) * mm, "end": v(14.36, -3.7) * mm});
            skLineSegment(sketch, "E9.8.0.42", {"start": v(22.43, -3.7) * mm, "end": v(27.06, -3.7) * mm});
            skLineSegment(sketch, "E9.8.0.43", {"start": v(73.23, -3.7) * mm, "end": v(77.86, -3.7) * mm});
            skLineSegment(sketch, "E9.8.0.44", {"start": v(115.96, 0.92) * mm, "end": v(115.96, -3.7) * mm});
            skLineSegment(sketch, "E9.8.0.45", {"start": v(60.53, 0.92) * mm, "end": v(65.16, 0.92) * mm});
            skLineSegment(sketch, "E9.8.0.46", {"start": v(111.33, 0.92) * mm, "end": v(115.96, 0.92) * mm});
            skLineSegment(sketch, "E9.8.0.47", {"start": v(-15.67, 0.92) * mm, "end": v(-11.04, 0.92) * mm});
            skLineSegment(sketch, "E9.8.0.48", {"start": v(35.13, 0.92) * mm, "end": v(39.76, 0.92) * mm});
            skLineSegment(sketch, "E9.8.0.49", {"start": v(-23.74, 0.92) * mm, "end": v(-23.74, -3.7) * mm});
            skLineSegment(sketch, "E9.8.0.50", {"start": v(85.93, 0.92) * mm, "end": v(90.56, 0.92) * mm});
            skLineSegment(sketch, "E9.8.0.51", {"start": v(65.16, 0.92) * mm, "end": v(65.16, -3.7) * mm});
            skLineSegment(sketch, "E9.8.0.52", {"start": v(52.46, 0.92) * mm, "end": v(52.46, -3.7) * mm});
            skLineSegment(sketch, "E9.8.0.53", {"start": v(103.26, 0.92) * mm, "end": v(103.26, -3.7) * mm});
            skLineSegment(sketch, "E9.8.0.54", {"start": v(-15.67, -3.7) * mm, "end": v(-11.04, -3.7) * mm});
            skLineSegment(sketch, "E9.8.0.55", {"start": v(111.33, 0.92) * mm, "end": v(111.33, -3.7) * mm});
            skLineSegment(sketch, "E9.8.0.56", {"start": v(60.53, 0.92) * mm, "end": v(60.53, -3.7) * mm});
            skLineSegment(sketch, "E9.8.0.57", {"start": v(85.93, -3.7) * mm, "end": v(90.56, -3.7) * mm});
            skLineSegment(sketch, "E9.8.0.58", {"start": v(35.13, -3.7) * mm, "end": v(39.76, -3.7) * mm});
            skLineSegment(sketch, "E9.8.0.59", {"start": v(9.73, 0.92) * mm, "end": v(9.73, -3.7) * mm});
            skLineSegment(sketch, "E9.8.0.60", {"start": v(-36.44, 0.92) * mm, "end": v(-36.44, -3.7) * mm});
            skLineSegment(sketch, "E9.8.0.61", {"start": v(-41.07, -3.7) * mm, "end": v(-36.44, -3.7) * mm});
            skLineSegment(sketch, "E9.8.0.62", {"start": v(-79.17, -3.7) * mm, "end": v(-74.54, -3.7) * mm});
            skLineSegment(sketch, "E9.8.0.63", {"start": v(-66.47, -3.7) * mm, "end": v(-61.84, -3.7) * mm});
            skLineSegment(sketch, "E9.8.0.64", {"start": v(-66.47, 0.92) * mm, "end": v(-66.47, -3.7) * mm});
            skLineSegment(sketch, "E9.8.0.65", {"start": v(-61.84, 0.92) * mm, "end": v(-61.84, -3.7) * mm});
            skLineSegment(sketch, "E9.8.0.66", {"start": v(-53.77, 0.92) * mm, "end": v(-53.77, -3.7) * mm});
            skLineSegment(sketch, "E9.8.0.67", {"start": v(-2.97, 0.92) * mm, "end": v(-2.97, -3.7) * mm});
            skLineSegment(sketch, "E9.8.0.68", {"start": v(22.43, 0.92) * mm, "end": v(22.43, -3.7) * mm});
            skLineSegment(sketch, "E9.8.0.69", {"start": v(-49.14, 0.92) * mm, "end": v(-49.14, -3.7) * mm});
            skLineSegment(sketch, "E9.8.0.70", {"start": v(1.66, 0.92) * mm, "end": v(1.66, -3.7) * mm});
            skLineSegment(sketch, "E9.8.0.71", {"start": v(77.86, 0.92) * mm, "end": v(77.86, -3.7) * mm});
            skLineSegment(sketch, "E9.8.0.72", {"start": v(27.06, 0.92) * mm, "end": v(27.06, -3.7) * mm});
            skLineSegment(sketch, "E9.8.0.73", {"start": v(-41.07, 0.92) * mm, "end": v(-36.44, 0.92) * mm});
            skLineSegment(sketch, "E9.8.0.74", {"start": v(-28.37, -3.7) * mm, "end": v(-23.74, -3.7) * mm});
            skLineSegment(sketch, "E9.8.0.75", {"start": v(-28.37, 0.92) * mm, "end": v(-23.74, 0.92) * mm});
            skLineSegment(sketch, "E9.8.0.76", {"start": v(22.43, 0.92) * mm, "end": v(27.06, 0.92) * mm});
            skLineSegment(sketch, "E9.8.0.77", {"start": v(73.23, 0.92) * mm, "end": v(77.86, 0.92) * mm});
            skLineSegment(sketch, "E9.8.0.78", {"start": v(-2.97, 0.92) * mm, "end": v(1.66, 0.92) * mm});
            skLineSegment(sketch, "E9.8.0.79", {"start": v(47.83, 0.92) * mm, "end": v(52.46, 0.92) * mm});
            skLineSegment(sketch, "E9.8.0.80", {"start": v(98.63, 0.92) * mm, "end": v(103.26, 0.92) * mm});
            skLineSegment(sketch, "E9.8.0.81", {"start": v(-53.77, 0.92) * mm, "end": v(-49.14, 0.92) * mm});
            skPoint(sketch, "E9.9.0.0", {"position": v(-79.15, -14.09) * mm});
            skPoint(sketch, "E9.9.0.1", {"position": v(88.26, -11.78) * mm});
            skPoint(sketch, "E9.9.0.2", {"position": v(37.46, -11.78) * mm});
            skPoint(sketch, "E9.9.0.3", {"position": v(-51.44, -11.78) * mm});
            skPoint(sketch, "E9.9.0.4", {"position": v(113.66, -11.78) * mm});
            skPoint(sketch, "E9.9.0.5", {"position": v(-64.14, -11.78) * mm});
            skPoint(sketch, "E9.9.0.6", {"position": v(24.76, -11.78) * mm});
            skPoint(sketch, "E9.9.0.7", {"position": v(12.06, -11.78) * mm});
            skLineSegment(sketch, "E9.9.0.8", {"start": v(-76.84, -11.78) * mm, "end": v(-51.44, -11.78) * mm, "construction": true});
            skPoint(sketch, "E9.9.0.9", {"position": v(-76.84, -11.78) * mm});
            skPoint(sketch, "E9.9.0.10", {"position": v(-13.34, -11.78) * mm});
            skPoint(sketch, "E9.9.0.11", {"position": v(50.16, -11.78) * mm});
            skPoint(sketch, "E9.9.0.12", {"position": v(-38.74, -11.78) * mm});
            skPoint(sketch, "E9.9.0.13", {"position": v(62.86, -11.78) * mm});
            skPoint(sketch, "E9.9.0.14", {"position": v(-26.04, -11.78) * mm});
            skPoint(sketch, "E9.9.0.15", {"position": v(75.56, -11.78) * mm});
            skPoint(sketch, "E9.9.0.16", {"position": v(-0.64, -11.78) * mm});
            skPoint(sketch, "E9.9.0.17", {"position": v(100.96, -11.78) * mm});
            skLineSegment(sketch, "E9.9.0.18", {"start": v(90.57, -11.78) * mm, "end": v(90.57, -16.4) * mm});
            skLineSegment(sketch, "E9.9.0.19", {"start": v(47.85, -11.78) * mm, "end": v(47.85, -16.4) * mm});
            skLineSegment(sketch, "E9.9.0.20", {"start": v(-28.35, -11.78) * mm, "end": v(-28.35, -16.4) * mm});
            skLineSegment(sketch, "E9.9.0.21", {"start": v(73.25, -11.78) * mm, "end": v(73.25, -16.4) * mm});
            skLineSegment(sketch, "E9.9.0.22", {"start": v(9.75, -16.4) * mm, "end": v(14.37, -16.4) * mm});
            skLineSegment(sketch, "E9.9.0.23", {"start": v(98.65, -11.78) * mm, "end": v(98.65, -16.4) * mm});
            skLineSegment(sketch, "E9.9.0.24", {"start": v(39.77, -11.78) * mm, "end": v(39.77, -16.4) * mm});
            skLineSegment(sketch, "E9.9.0.25", {"start": v(-15.65, -11.78) * mm, "end": v(-15.65, -16.4) * mm});
            skLineSegment(sketch, "E9.9.0.26", {"start": v(60.55, -16.4) * mm, "end": v(65.17, -16.4) * mm});
            skLineSegment(sketch, "E9.9.0.27", {"start": v(35.15, -11.78) * mm, "end": v(35.15, -16.4) * mm});
            skLineSegment(sketch, "E9.9.0.28", {"start": v(85.95, -11.78) * mm, "end": v(85.95, -16.4) * mm});
            skLineSegment(sketch, "E9.9.0.29", {"start": v(-53.75, -16.4) * mm, "end": v(-49.13, -16.4) * mm});
            skLineSegment(sketch, "E9.9.0.30", {"start": v(-66.45, -11.78) * mm, "end": v(-61.83, -11.78) * mm});
            skLineSegment(sketch, "E9.9.0.31", {"start": v(111.35, -16.4) * mm, "end": v(115.97, -16.4) * mm});
            skLineSegment(sketch, "E9.9.0.32", {"start": v(-74.53, -11.78) * mm, "end": v(-74.53, -16.4) * mm});
            skLineSegment(sketch, "E9.9.0.33", {"start": v(-79.15, -11.78) * mm, "end": v(-79.15, -16.4) * mm});
            skLineSegment(sketch, "E9.9.0.34", {"start": v(-79.15, -11.78) * mm, "end": v(-74.53, -11.78) * mm});
            skLineSegment(sketch, "E9.9.0.35", {"start": v(-41.05, -11.78) * mm, "end": v(-41.05, -16.4) * mm});
            skLineSegment(sketch, "E9.9.0.36", {"start": v(-11.03, -11.78) * mm, "end": v(-11.03, -16.4) * mm});
            skLineSegment(sketch, "E9.9.0.37", {"start": v(-2.95, -16.4) * mm, "end": v(1.67, -16.4) * mm});
            skLineSegment(sketch, "E9.9.0.38", {"start": v(47.85, -16.4) * mm, "end": v(52.47, -16.4) * mm});
            skLineSegment(sketch, "E9.9.0.39", {"start": v(98.65, -16.4) * mm, "end": v(103.27, -16.4) * mm});
            skLineSegment(sketch, "E9.9.0.40", {"start": v(9.75, -11.78) * mm, "end": v(14.37, -11.78) * mm});
            skLineSegment(sketch, "E9.9.0.41", {"start": v(14.37, -11.78) * mm, "end": v(14.37, -16.4) * mm});
            skLineSegment(sketch, "E9.9.0.42", {"start": v(22.45, -16.4) * mm, "end": v(27.07, -16.4) * mm});
            skLineSegment(sketch, "E9.9.0.43", {"start": v(73.25, -16.4) * mm, "end": v(77.87, -16.4) * mm});
            skLineSegment(sketch, "E9.9.0.44", {"start": v(115.97, -11.78) * mm, "end": v(115.97, -16.4) * mm});
            skLineSegment(sketch, "E9.9.0.45", {"start": v(60.55, -11.78) * mm, "end": v(65.17, -11.78) * mm});
            skLineSegment(sketch, "E9.9.0.46", {"start": v(111.35, -11.78) * mm, "end": v(115.97, -11.78) * mm});
            skLineSegment(sketch, "E9.9.0.47", {"start": v(-15.65, -11.78) * mm, "end": v(-11.03, -11.78) * mm});
            skLineSegment(sketch, "E9.9.0.48", {"start": v(35.15, -11.78) * mm, "end": v(39.77, -11.78) * mm});
            skLineSegment(sketch, "E9.9.0.49", {"start": v(-23.73, -11.78) * mm, "end": v(-23.73, -16.4) * mm});
            skLineSegment(sketch, "E9.9.0.50", {"start": v(85.95, -11.78) * mm, "end": v(90.57, -11.78) * mm});
            skLineSegment(sketch, "E9.9.0.51", {"start": v(65.17, -11.78) * mm, "end": v(65.17, -16.4) * mm});
            skLineSegment(sketch, "E9.9.0.52", {"start": v(52.47, -11.78) * mm, "end": v(52.47, -16.4) * mm});
            skLineSegment(sketch, "E9.9.0.53", {"start": v(103.27, -11.78) * mm, "end": v(103.27, -16.4) * mm});
            skLineSegment(sketch, "E9.9.0.54", {"start": v(-15.65, -16.4) * mm, "end": v(-11.03, -16.4) * mm});
            skLineSegment(sketch, "E9.9.0.55", {"start": v(111.35, -11.78) * mm, "end": v(111.35, -16.4) * mm});
            skLineSegment(sketch, "E9.9.0.56", {"start": v(60.55, -11.78) * mm, "end": v(60.55, -16.4) * mm});
            skLineSegment(sketch, "E9.9.0.57", {"start": v(85.95, -16.4) * mm, "end": v(90.57, -16.4) * mm});
            skLineSegment(sketch, "E9.9.0.58", {"start": v(35.15, -16.4) * mm, "end": v(39.77, -16.4) * mm});
            skLineSegment(sketch, "E9.9.0.59", {"start": v(9.75, -11.78) * mm, "end": v(9.75, -16.4) * mm});
            skLineSegment(sketch, "E9.9.0.60", {"start": v(-36.43, -11.78) * mm, "end": v(-36.43, -16.4) * mm});
            skLineSegment(sketch, "E9.9.0.61", {"start": v(-41.05, -16.4) * mm, "end": v(-36.43, -16.4) * mm});
            skLineSegment(sketch, "E9.9.0.62", {"start": v(-79.15, -16.4) * mm, "end": v(-74.53, -16.4) * mm});
            skLineSegment(sketch, "E9.9.0.63", {"start": v(-66.45, -16.4) * mm, "end": v(-61.83, -16.4) * mm});
            skLineSegment(sketch, "E9.9.0.64", {"start": v(-66.45, -11.78) * mm, "end": v(-66.45, -16.4) * mm});
            skLineSegment(sketch, "E9.9.0.65", {"start": v(-61.83, -11.78) * mm, "end": v(-61.83, -16.4) * mm});
            skLineSegment(sketch, "E9.9.0.66", {"start": v(-53.75, -11.78) * mm, "end": v(-53.75, -16.4) * mm});
            skLineSegment(sketch, "E9.9.0.67", {"start": v(-2.95, -11.78) * mm, "end": v(-2.95, -16.4) * mm});
            skLineSegment(sketch, "E9.9.0.68", {"start": v(22.45, -11.78) * mm, "end": v(22.45, -16.4) * mm});
            skLineSegment(sketch, "E9.9.0.69", {"start": v(-49.13, -11.78) * mm, "end": v(-49.13, -16.4) * mm});
            skLineSegment(sketch, "E9.9.0.70", {"start": v(1.67, -11.78) * mm, "end": v(1.67, -16.4) * mm});
            skLineSegment(sketch, "E9.9.0.71", {"start": v(77.87, -11.78) * mm, "end": v(77.87, -16.4) * mm});
            skLineSegment(sketch, "E9.9.0.72", {"start": v(27.07, -11.78) * mm, "end": v(27.07, -16.4) * mm});
            skLineSegment(sketch, "E9.9.0.73", {"start": v(-41.05, -11.78) * mm, "end": v(-36.43, -11.78) * mm});
            skLineSegment(sketch, "E9.9.0.74", {"start": v(-28.35, -16.4) * mm, "end": v(-23.73, -16.4) * mm});
            skLineSegment(sketch, "E9.9.0.75", {"start": v(-28.35, -11.78) * mm, "end": v(-23.73, -11.78) * mm});
            skLineSegment(sketch, "E9.9.0.76", {"start": v(22.45, -11.78) * mm, "end": v(27.07, -11.78) * mm});
            skLineSegment(sketch, "E9.9.0.77", {"start": v(73.25, -11.78) * mm, "end": v(77.87, -11.78) * mm});
            skLineSegment(sketch, "E9.9.0.78", {"start": v(-2.95, -11.78) * mm, "end": v(1.67, -11.78) * mm});
            skLineSegment(sketch, "E9.9.0.79", {"start": v(47.85, -11.78) * mm, "end": v(52.47, -11.78) * mm});
            skLineSegment(sketch, "E9.9.0.80", {"start": v(98.65, -11.78) * mm, "end": v(103.27, -11.78) * mm});
            skLineSegment(sketch, "E9.9.0.81", {"start": v(-53.75, -11.78) * mm, "end": v(-49.13, -11.78) * mm});
            skPoint(sketch, "E9.10.0.0", {"position": v(-79.14, -26.79) * mm});
            skPoint(sketch, "E9.10.0.1", {"position": v(88.27, -24.48) * mm});
            skPoint(sketch, "E9.10.0.2", {"position": v(37.47, -24.48) * mm});
            skPoint(sketch, "E9.10.0.3", {"position": v(-51.43, -24.48) * mm});
            skPoint(sketch, "E9.10.0.4", {"position": v(113.67, -24.48) * mm});
            skPoint(sketch, "E9.10.0.5", {"position": v(-64.13, -24.48) * mm});
            skPoint(sketch, "E9.10.0.6", {"position": v(24.77, -24.48) * mm});
            skPoint(sketch, "E9.10.0.7", {"position": v(12.07, -24.48) * mm});
            skLineSegment(sketch, "E9.10.0.8", {"start": v(-76.83, -24.48) * mm, "end": v(-51.43, -24.48) * mm, "construction": true});
            skPoint(sketch, "E9.10.0.9", {"position": v(-76.83, -24.48) * mm});
            skPoint(sketch, "E9.10.0.10", {"position": v(-13.33, -24.48) * mm});
            skPoint(sketch, "E9.10.0.11", {"position": v(50.17, -24.48) * mm});
            skPoint(sketch, "E9.10.0.12", {"position": v(-38.73, -24.48) * mm});
            skPoint(sketch, "E9.10.0.13", {"position": v(62.87, -24.48) * mm});
            skPoint(sketch, "E9.10.0.14", {"position": v(-26.03, -24.48) * mm});
            skPoint(sketch, "E9.10.0.15", {"position": v(75.57, -24.48) * mm});
            skPoint(sketch, "E9.10.0.16", {"position": v(-0.63, -24.48) * mm});
            skPoint(sketch, "E9.10.0.17", {"position": v(100.97, -24.48) * mm});
            skLineSegment(sketch, "E9.10.0.18", {"start": v(90.58, -24.48) * mm, "end": v(90.58, -29.1) * mm});
            skLineSegment(sketch, "E9.10.0.19", {"start": v(47.86, -24.48) * mm, "end": v(47.86, -29.1) * mm});
            skLineSegment(sketch, "E9.10.0.20", {"start": v(-28.34, -24.48) * mm, "end": v(-28.34, -29.1) * mm});
            skLineSegment(sketch, "E9.10.0.21", {"start": v(73.26, -24.48) * mm, "end": v(73.26, -29.1) * mm});
            skLineSegment(sketch, "E9.10.0.22", {"start": v(9.76, -29.1) * mm, "end": v(14.38, -29.1) * mm});
            skLineSegment(sketch, "E9.10.0.23", {"start": v(98.66, -24.48) * mm, "end": v(98.66, -29.1) * mm});
            skLineSegment(sketch, "E9.10.0.24", {"start": v(39.78, -24.48) * mm, "end": v(39.78, -29.1) * mm});
            skLineSegment(sketch, "E9.10.0.25", {"start": v(-15.64, -24.48) * mm, "end": v(-15.64, -29.1) * mm});
            skLineSegment(sketch, "E9.10.0.26", {"start": v(60.56, -29.1) * mm, "end": v(65.18, -29.1) * mm});
            skLineSegment(sketch, "E9.10.0.27", {"start": v(35.16, -24.48) * mm, "end": v(35.16, -29.1) * mm});
            skLineSegment(sketch, "E9.10.0.28", {"start": v(85.96, -24.48) * mm, "end": v(85.96, -29.1) * mm});
            skLineSegment(sketch, "E9.10.0.29", {"start": v(-53.74, -29.1) * mm, "end": v(-49.12, -29.1) * mm});
            skLineSegment(sketch, "E9.10.0.30", {"start": v(-66.44, -24.48) * mm, "end": v(-61.82, -24.48) * mm});
            skLineSegment(sketch, "E9.10.0.31", {"start": v(111.36, -29.1) * mm, "end": v(115.98, -29.1) * mm});
            skLineSegment(sketch, "E9.10.0.32", {"start": v(-74.52, -24.48) * mm, "end": v(-74.52, -29.1) * mm});
            skLineSegment(sketch, "E9.10.0.33", {"start": v(-79.14, -24.48) * mm, "end": v(-79.14, -29.1) * mm});
            skLineSegment(sketch, "E9.10.0.34", {"start": v(-79.14, -24.48) * mm, "end": v(-74.52, -24.48) * mm});
            skLineSegment(sketch, "E9.10.0.35", {"start": v(-41.04, -24.48) * mm, "end": v(-41.04, -29.1) * mm});
            skLineSegment(sketch, "E9.10.0.36", {"start": v(-11.02, -24.48) * mm, "end": v(-11.02, -29.1) * mm});
            skLineSegment(sketch, "E9.10.0.37", {"start": v(-2.94, -29.1) * mm, "end": v(1.68, -29.1) * mm});
            skLineSegment(sketch, "E9.10.0.38", {"start": v(47.86, -29.1) * mm, "end": v(52.48, -29.1) * mm});
            skLineSegment(sketch, "E9.10.0.39", {"start": v(98.66, -29.1) * mm, "end": v(103.28, -29.1) * mm});
            skLineSegment(sketch, "E9.10.0.40", {"start": v(9.76, -24.48) * mm, "end": v(14.38, -24.48) * mm});
            skLineSegment(sketch, "E9.10.0.41", {"start": v(14.38, -24.48) * mm, "end": v(14.38, -29.1) * mm});
            skLineSegment(sketch, "E9.10.0.42", {"start": v(22.46, -29.1) * mm, "end": v(27.08, -29.1) * mm});
            skLineSegment(sketch, "E9.10.0.43", {"start": v(73.26, -29.1) * mm, "end": v(77.88, -29.1) * mm});
            skLineSegment(sketch, "E9.10.0.44", {"start": v(115.98, -24.48) * mm, "end": v(115.98, -29.1) * mm});
            skLineSegment(sketch, "E9.10.0.45", {"start": v(60.56, -24.48) * mm, "end": v(65.18, -24.48) * mm});
            skLineSegment(sketch, "E9.10.0.46", {"start": v(111.36, -24.48) * mm, "end": v(115.98, -24.48) * mm});
            skLineSegment(sketch, "E9.10.0.47", {"start": v(-15.64, -24.48) * mm, "end": v(-11.02, -24.48) * mm});
            skLineSegment(sketch, "E9.10.0.48", {"start": v(35.16, -24.48) * mm, "end": v(39.78, -24.48) * mm});
            skLineSegment(sketch, "E9.10.0.49", {"start": v(-23.72, -24.48) * mm, "end": v(-23.72, -29.1) * mm});
            skLineSegment(sketch, "E9.10.0.50", {"start": v(85.96, -24.48) * mm, "end": v(90.58, -24.48) * mm});
            skLineSegment(sketch, "E9.10.0.51", {"start": v(65.18, -24.48) * mm, "end": v(65.18, -29.1) * mm});
            skLineSegment(sketch, "E9.10.0.52", {"start": v(52.48, -24.48) * mm, "end": v(52.48, -29.1) * mm});
            skLineSegment(sketch, "E9.10.0.53", {"start": v(103.28, -24.48) * mm, "end": v(103.28, -29.1) * mm});
            skLineSegment(sketch, "E9.10.0.54", {"start": v(-15.64, -29.1) * mm, "end": v(-11.02, -29.1) * mm});
            skLineSegment(sketch, "E9.10.0.55", {"start": v(111.36, -24.48) * mm, "end": v(111.36, -29.1) * mm});
            skLineSegment(sketch, "E9.10.0.56", {"start": v(60.56, -24.48) * mm, "end": v(60.56, -29.1) * mm});
            skLineSegment(sketch, "E9.10.0.57", {"start": v(85.96, -29.1) * mm, "end": v(90.58, -29.1) * mm});
            skLineSegment(sketch, "E9.10.0.58", {"start": v(35.16, -29.1) * mm, "end": v(39.78, -29.1) * mm});
            skLineSegment(sketch, "E9.10.0.59", {"start": v(9.76, -24.48) * mm, "end": v(9.76, -29.1) * mm});
            skLineSegment(sketch, "E9.10.0.60", {"start": v(-36.42, -24.48) * mm, "end": v(-36.42, -29.1) * mm});
            skLineSegment(sketch, "E9.10.0.61", {"start": v(-41.04, -29.1) * mm, "end": v(-36.42, -29.1) * mm});
            skLineSegment(sketch, "E9.10.0.62", {"start": v(-79.14, -29.1) * mm, "end": v(-74.52, -29.1) * mm});
            skLineSegment(sketch, "E9.10.0.63", {"start": v(-66.44, -29.1) * mm, "end": v(-61.82, -29.1) * mm});
            skLineSegment(sketch, "E9.10.0.64", {"start": v(-66.44, -24.48) * mm, "end": v(-66.44, -29.1) * mm});
            skLineSegment(sketch, "E9.10.0.65", {"start": v(-61.82, -24.48) * mm, "end": v(-61.82, -29.1) * mm});
            skLineSegment(sketch, "E9.10.0.66", {"start": v(-53.74, -24.48) * mm, "end": v(-53.74, -29.1) * mm});
            skLineSegment(sketch, "E9.10.0.67", {"start": v(-2.94, -24.48) * mm, "end": v(-2.94, -29.1) * mm});
            skLineSegment(sketch, "E9.10.0.68", {"start": v(22.46, -24.48) * mm, "end": v(22.46, -29.1) * mm});
            skLineSegment(sketch, "E9.10.0.69", {"start": v(-49.12, -24.48) * mm, "end": v(-49.12, -29.1) * mm});
            skLineSegment(sketch, "E9.10.0.70", {"start": v(1.68, -24.48) * mm, "end": v(1.68, -29.1) * mm});
            skLineSegment(sketch, "E9.10.0.71", {"start": v(77.88, -24.48) * mm, "end": v(77.88, -29.1) * mm});
            skLineSegment(sketch, "E9.10.0.72", {"start": v(27.08, -24.48) * mm, "end": v(27.08, -29.1) * mm});
            skLineSegment(sketch, "E9.10.0.73", {"start": v(-41.04, -24.48) * mm, "end": v(-36.42, -24.48) * mm});
            skLineSegment(sketch, "E9.10.0.74", {"start": v(-28.34, -29.1) * mm, "end": v(-23.72, -29.1) * mm});
            skLineSegment(sketch, "E9.10.0.75", {"start": v(-28.34, -24.48) * mm, "end": v(-23.72, -24.48) * mm});
            skLineSegment(sketch, "E9.10.0.76", {"start": v(22.46, -24.48) * mm, "end": v(27.08, -24.48) * mm});
            skLineSegment(sketch, "E9.10.0.77", {"start": v(73.26, -24.48) * mm, "end": v(77.88, -24.48) * mm});
            skLineSegment(sketch, "E9.10.0.78", {"start": v(-2.94, -24.48) * mm, "end": v(1.68, -24.48) * mm});
            skLineSegment(sketch, "E9.10.0.79", {"start": v(47.86, -24.48) * mm, "end": v(52.48, -24.48) * mm});
            skLineSegment(sketch, "E9.10.0.80", {"start": v(98.66, -24.48) * mm, "end": v(103.28, -24.48) * mm});
            skLineSegment(sketch, "E9.10.0.81", {"start": v(-53.74, -24.48) * mm, "end": v(-49.12, -24.48) * mm});
            skPoint(sketch, "E9.11.0.0", {"position": v(-79.13, -39.49) * mm});
            skPoint(sketch, "E9.11.0.1", {"position": v(88.28, -37.18) * mm});
            skPoint(sketch, "E9.11.0.2", {"position": v(37.48, -37.18) * mm});
            skPoint(sketch, "E9.11.0.3", {"position": v(-51.42, -37.18) * mm});
            skPoint(sketch, "E9.11.0.4", {"position": v(113.68, -37.18) * mm});
            skPoint(sketch, "E9.11.0.5", {"position": v(-64.12, -37.18) * mm});
            skPoint(sketch, "E9.11.0.6", {"position": v(24.78, -37.18) * mm});
            skPoint(sketch, "E9.11.0.7", {"position": v(12.08, -37.18) * mm});
            skLineSegment(sketch, "E9.11.0.8", {"start": v(-76.82, -37.18) * mm, "end": v(-51.42, -37.18) * mm, "construction": true});
            skPoint(sketch, "E9.11.0.9", {"position": v(-76.82, -37.18) * mm});
            skPoint(sketch, "E9.11.0.10", {"position": v(-13.32, -37.18) * mm});
            skPoint(sketch, "E9.11.0.11", {"position": v(50.18, -37.18) * mm});
            skPoint(sketch, "E9.11.0.12", {"position": v(-38.72, -37.18) * mm});
            skPoint(sketch, "E9.11.0.13", {"position": v(62.88, -37.18) * mm});
            skPoint(sketch, "E9.11.0.14", {"position": v(-26.02, -37.18) * mm});
            skPoint(sketch, "E9.11.0.15", {"position": v(75.58, -37.18) * mm});
            skPoint(sketch, "E9.11.0.16", {"position": v(-0.62, -37.18) * mm});
            skPoint(sketch, "E9.11.0.17", {"position": v(100.98, -37.18) * mm});
            skLineSegment(sketch, "E9.11.0.18", {"start": v(90.6, -37.18) * mm, "end": v(90.6, -41.8) * mm});
            skLineSegment(sketch, "E9.11.0.19", {"start": v(47.87, -37.18) * mm, "end": v(47.87, -41.8) * mm});
            skLineSegment(sketch, "E9.11.0.20", {"start": v(-28.33, -37.18) * mm, "end": v(-28.33, -41.8) * mm});
            skLineSegment(sketch, "E9.11.0.21", {"start": v(73.27, -37.18) * mm, "end": v(73.27, -41.8) * mm});
            skLineSegment(sketch, "E9.11.0.22", {"start": v(9.77, -41.8) * mm, "end": v(14.4, -41.8) * mm});
            skLineSegment(sketch, "E9.11.0.23", {"start": v(98.67, -37.18) * mm, "end": v(98.67, -41.8) * mm});
            skLineSegment(sketch, "E9.11.0.24", {"start": v(39.8, -37.18) * mm, "end": v(39.8, -41.8) * mm});
            skLineSegment(sketch, "E9.11.0.25", {"start": v(-15.63, -37.18) * mm, "end": v(-15.63, -41.8) * mm});
            skLineSegment(sketch, "E9.11.0.26", {"start": v(60.57, -41.8) * mm, "end": v(65.2, -41.8) * mm});
            skLineSegment(sketch, "E9.11.0.27", {"start": v(35.17, -37.18) * mm, "end": v(35.17, -41.8) * mm});
            skLineSegment(sketch, "E9.11.0.28", {"start": v(85.97, -37.18) * mm, "end": v(85.97, -41.8) * mm});
            skLineSegment(sketch, "E9.11.0.29", {"start": v(-53.73, -41.8) * mm, "end": v(-49.1, -41.8) * mm});
            skLineSegment(sketch, "E9.11.0.30", {"start": v(-66.43, -37.18) * mm, "end": v(-61.8, -37.18) * mm});
            skLineSegment(sketch, "E9.11.0.31", {"start": v(111.37, -41.8) * mm, "end": v(116, -41.8) * mm});
            skLineSegment(sketch, "E9.11.0.32", {"start": v(-74.5, -37.18) * mm, "end": v(-74.5, -41.8) * mm});
            skLineSegment(sketch, "E9.11.0.33", {"start": v(-79.13, -37.18) * mm, "end": v(-79.13, -41.8) * mm});
            skLineSegment(sketch, "E9.11.0.34", {"start": v(-79.13, -37.18) * mm, "end": v(-74.5, -37.18) * mm});
            skLineSegment(sketch, "E9.11.0.35", {"start": v(-41.03, -37.18) * mm, "end": v(-41.03, -41.8) * mm});
            skLineSegment(sketch, "E9.11.0.36", {"start": v(-11, -37.18) * mm, "end": v(-11, -41.8) * mm});
            skLineSegment(sketch, "E9.11.0.37", {"start": v(-2.93, -41.8) * mm, "end": v(1.7, -41.8) * mm});
            skLineSegment(sketch, "E9.11.0.38", {"start": v(47.87, -41.8) * mm, "end": v(52.5, -41.8) * mm});
            skLineSegment(sketch, "E9.11.0.39", {"start": v(98.67, -41.8) * mm, "end": v(103.3, -41.8) * mm});
            skLineSegment(sketch, "E9.11.0.40", {"start": v(9.77, -37.18) * mm, "end": v(14.4, -37.18) * mm});
            skLineSegment(sketch, "E9.11.0.41", {"start": v(14.4, -37.18) * mm, "end": v(14.4, -41.8) * mm});
            skLineSegment(sketch, "E9.11.0.42", {"start": v(22.47, -41.8) * mm, "end": v(27.1, -41.8) * mm});
            skLineSegment(sketch, "E9.11.0.43", {"start": v(73.27, -41.8) * mm, "end": v(77.9, -41.8) * mm});
            skLineSegment(sketch, "E9.11.0.44", {"start": v(116, -37.18) * mm, "end": v(116, -41.8) * mm});
            skLineSegment(sketch, "E9.11.0.45", {"start": v(60.57, -37.18) * mm, "end": v(65.2, -37.18) * mm});
            skLineSegment(sketch, "E9.11.0.46", {"start": v(111.37, -37.18) * mm, "end": v(116, -37.18) * mm});
            skLineSegment(sketch, "E9.11.0.47", {"start": v(-15.63, -37.18) * mm, "end": v(-11, -37.18) * mm});
            skLineSegment(sketch, "E9.11.0.48", {"start": v(35.17, -37.18) * mm, "end": v(39.8, -37.18) * mm});
            skLineSegment(sketch, "E9.11.0.49", {"start": v(-23.7, -37.18) * mm, "end": v(-23.7, -41.8) * mm});
            skLineSegment(sketch, "E9.11.0.50", {"start": v(85.97, -37.18) * mm, "end": v(90.6, -37.18) * mm});
            skLineSegment(sketch, "E9.11.0.51", {"start": v(65.2, -37.18) * mm, "end": v(65.2, -41.8) * mm});
            skLineSegment(sketch, "E9.11.0.52", {"start": v(52.5, -37.18) * mm, "end": v(52.5, -41.8) * mm});
            skLineSegment(sketch, "E9.11.0.53", {"start": v(103.3, -37.18) * mm, "end": v(103.3, -41.8) * mm});
            skLineSegment(sketch, "E9.11.0.54", {"start": v(-15.63, -41.8) * mm, "end": v(-11, -41.8) * mm});
            skLineSegment(sketch, "E9.11.0.55", {"start": v(111.37, -37.18) * mm, "end": v(111.37, -41.8) * mm});
            skLineSegment(sketch, "E9.11.0.56", {"start": v(60.57, -37.18) * mm, "end": v(60.57, -41.8) * mm});
            skLineSegment(sketch, "E9.11.0.57", {"start": v(85.97, -41.8) * mm, "end": v(90.6, -41.8) * mm});
            skLineSegment(sketch, "E9.11.0.58", {"start": v(35.17, -41.8) * mm, "end": v(39.8, -41.8) * mm});
            skLineSegment(sketch, "E9.11.0.59", {"start": v(9.77, -37.18) * mm, "end": v(9.77, -41.8) * mm});
            skLineSegment(sketch, "E9.11.0.60", {"start": v(-36.4, -37.18) * mm, "end": v(-36.4, -41.8) * mm});
            skLineSegment(sketch, "E9.11.0.61", {"start": v(-41.03, -41.8) * mm, "end": v(-36.4, -41.8) * mm});
            skLineSegment(sketch, "E9.11.0.62", {"start": v(-79.13, -41.8) * mm, "end": v(-74.5, -41.8) * mm});
            skLineSegment(sketch, "E9.11.0.63", {"start": v(-66.43, -41.8) * mm, "end": v(-61.8, -41.8) * mm});
            skLineSegment(sketch, "E9.11.0.64", {"start": v(-66.43, -37.18) * mm, "end": v(-66.43, -41.8) * mm});
            skLineSegment(sketch, "E9.11.0.65", {"start": v(-61.8, -37.18) * mm, "end": v(-61.8, -41.8) * mm});
            skLineSegment(sketch, "E9.11.0.66", {"start": v(-53.73, -37.18) * mm, "end": v(-53.73, -41.8) * mm});
            skLineSegment(sketch, "E9.11.0.67", {"start": v(-2.93, -37.18) * mm, "end": v(-2.93, -41.8) * mm});
            skLineSegment(sketch, "E9.11.0.68", {"start": v(22.47, -37.18) * mm, "end": v(22.47, -41.8) * mm});
            skLineSegment(sketch, "E9.11.0.69", {"start": v(-49.1, -37.18) * mm, "end": v(-49.1, -41.8) * mm});
            skLineSegment(sketch, "E9.11.0.70", {"start": v(1.7, -37.18) * mm, "end": v(1.7, -41.8) * mm});
            skLineSegment(sketch, "E9.11.0.71", {"start": v(77.9, -37.18) * mm, "end": v(77.9, -41.8) * mm});
            skLineSegment(sketch, "E9.11.0.72", {"start": v(27.1, -37.18) * mm, "end": v(27.1, -41.8) * mm});
            skLineSegment(sketch, "E9.11.0.73", {"start": v(-41.03, -37.18) * mm, "end": v(-36.4, -37.18) * mm});
            skLineSegment(sketch, "E9.11.0.74", {"start": v(-28.33, -41.8) * mm, "end": v(-23.7, -41.8) * mm});
            skLineSegment(sketch, "E9.11.0.75", {"start": v(-28.33, -37.18) * mm, "end": v(-23.7, -37.18) * mm});
            skLineSegment(sketch, "E9.11.0.76", {"start": v(22.47, -37.18) * mm, "end": v(27.1, -37.18) * mm});
            skLineSegment(sketch, "E9.11.0.77", {"start": v(73.27, -37.18) * mm, "end": v(77.9, -37.18) * mm});
            skLineSegment(sketch, "E9.11.0.78", {"start": v(-2.93, -37.18) * mm, "end": v(1.7, -37.18) * mm});
            skLineSegment(sketch, "E9.11.0.79", {"start": v(47.87, -37.18) * mm, "end": v(52.5, -37.18) * mm});
            skLineSegment(sketch, "E9.11.0.80", {"start": v(98.67, -37.18) * mm, "end": v(103.3, -37.18) * mm});
            skLineSegment(sketch, "E9.11.0.81", {"start": v(-53.73, -37.18) * mm, "end": v(-49.1, -37.18) * mm});
            skPoint(sketch, "E9.12.0.0", {"position": v(-79.12, -52.19) * mm});
            skPoint(sketch, "E9.12.0.1", {"position": v(88.3, -49.88) * mm});
            skPoint(sketch, "E9.12.0.2", {"position": v(37.5, -49.88) * mm});
            skPoint(sketch, "E9.12.0.3", {"position": v(-51.4, -49.88) * mm});
            skPoint(sketch, "E9.12.0.4", {"position": v(113.7, -49.88) * mm});
            skPoint(sketch, "E9.12.0.5", {"position": v(-64.1, -49.88) * mm});
            skPoint(sketch, "E9.12.0.6", {"position": v(24.8, -49.88) * mm});
            skPoint(sketch, "E9.12.0.7", {"position": v(12.1, -49.88) * mm});
            skLineSegment(sketch, "E9.12.0.8", {"start": v(-76.8, -49.88) * mm, "end": v(-51.4, -49.88) * mm, "construction": true});
            skPoint(sketch, "E9.12.0.9", {"position": v(-76.8, -49.88) * mm});
            skPoint(sketch, "E9.12.0.10", {"position": v(-13.3, -49.88) * mm});
            skPoint(sketch, "E9.12.0.11", {"position": v(50.2, -49.88) * mm});
            skPoint(sketch, "E9.12.0.12", {"position": v(-38.7, -49.88) * mm});
            skPoint(sketch, "E9.12.0.13", {"position": v(62.9, -49.88) * mm});
            skPoint(sketch, "E9.12.0.14", {"position": v(-26, -49.88) * mm});
            skPoint(sketch, "E9.12.0.15", {"position": v(75.6, -49.88) * mm});
            skPoint(sketch, "E9.12.0.16", {"position": v(-0.6, -49.88) * mm});
            skPoint(sketch, "E9.12.0.17", {"position": v(101, -49.88) * mm});
            skLineSegment(sketch, "E9.12.0.18", {"start": v(90.6, -49.88) * mm, "end": v(90.6, -54.5) * mm});
            skLineSegment(sketch, "E9.12.0.19", {"start": v(47.88, -49.88) * mm, "end": v(47.88, -54.5) * mm});
            skLineSegment(sketch, "E9.12.0.20", {"start": v(-28.32, -49.88) * mm, "end": v(-28.32, -54.5) * mm});
            skLineSegment(sketch, "E9.12.0.21", {"start": v(73.28, -49.88) * mm, "end": v(73.28, -54.5) * mm});
            skLineSegment(sketch, "E9.12.0.22", {"start": v(9.78, -54.5) * mm, "end": v(14.4, -54.5) * mm});
            skLineSegment(sketch, "E9.12.0.23", {"start": v(98.68, -49.88) * mm, "end": v(98.68, -54.5) * mm});
            skLineSegment(sketch, "E9.12.0.24", {"start": v(39.8, -49.88) * mm, "end": v(39.8, -54.5) * mm});
            skLineSegment(sketch, "E9.12.0.25", {"start": v(-15.62, -49.88) * mm, "end": v(-15.62, -54.5) * mm});
            skLineSegment(sketch, "E9.12.0.26", {"start": v(60.58, -54.5) * mm, "end": v(65.2, -54.5) * mm});
            skLineSegment(sketch, "E9.12.0.27", {"start": v(35.18, -49.88) * mm, "end": v(35.18, -54.5) * mm});
            skLineSegment(sketch, "E9.12.0.28", {"start": v(85.98, -49.88) * mm, "end": v(85.98, -54.5) * mm});
            skLineSegment(sketch, "E9.12.0.29", {"start": v(-53.72, -54.5) * mm, "end": v(-49.1, -54.5) * mm});
            skLineSegment(sketch, "E9.12.0.30", {"start": v(-66.42, -49.88) * mm, "end": v(-61.8, -49.88) * mm});
            skLineSegment(sketch, "E9.12.0.31", {"start": v(111.38, -54.5) * mm, "end": v(116, -54.5) * mm});
            skLineSegment(sketch, "E9.12.0.32", {"start": v(-74.5, -49.88) * mm, "end": v(-74.5, -54.5) * mm});
            skLineSegment(sketch, "E9.12.0.33", {"start": v(-79.12, -49.88) * mm, "end": v(-79.12, -54.5) * mm});
            skLineSegment(sketch, "E9.12.0.34", {"start": v(-79.12, -49.88) * mm, "end": v(-74.5, -49.88) * mm});
            skLineSegment(sketch, "E9.12.0.35", {"start": v(-41.02, -49.88) * mm, "end": v(-41.02, -54.5) * mm});
            skLineSegment(sketch, "E9.12.0.36", {"start": v(-11, -49.88) * mm, "end": v(-11, -54.5) * mm});
            skLineSegment(sketch, "E9.12.0.37", {"start": v(-2.92, -54.5) * mm, "end": v(1.7, -54.5) * mm});
            skLineSegment(sketch, "E9.12.0.38", {"start": v(47.88, -54.5) * mm, "end": v(52.5, -54.5) * mm});
            skLineSegment(sketch, "E9.12.0.39", {"start": v(98.68, -54.5) * mm, "end": v(103.3, -54.5) * mm});
            skLineSegment(sketch, "E9.12.0.40", {"start": v(9.78, -49.88) * mm, "end": v(14.4, -49.88) * mm});
            skLineSegment(sketch, "E9.12.0.41", {"start": v(14.4, -49.88) * mm, "end": v(14.4, -54.5) * mm});
            skLineSegment(sketch, "E9.12.0.42", {"start": v(22.48, -54.5) * mm, "end": v(27.1, -54.5) * mm});
            skLineSegment(sketch, "E9.12.0.43", {"start": v(73.28, -54.5) * mm, "end": v(77.9, -54.5) * mm});
            skLineSegment(sketch, "E9.12.0.44", {"start": v(116, -49.88) * mm, "end": v(116, -54.5) * mm});
            skLineSegment(sketch, "E9.12.0.45", {"start": v(60.58, -49.88) * mm, "end": v(65.2, -49.88) * mm});
            skLineSegment(sketch, "E9.12.0.46", {"start": v(111.38, -49.88) * mm, "end": v(116, -49.88) * mm});
            skLineSegment(sketch, "E9.12.0.47", {"start": v(-15.62, -49.88) * mm, "end": v(-11, -49.88) * mm});
            skLineSegment(sketch, "E9.12.0.48", {"start": v(35.18, -49.88) * mm, "end": v(39.8, -49.88) * mm});
            skLineSegment(sketch, "E9.12.0.49", {"start": v(-23.7, -49.88) * mm, "end": v(-23.7, -54.5) * mm});
            skLineSegment(sketch, "E9.12.0.50", {"start": v(85.98, -49.88) * mm, "end": v(90.6, -49.88) * mm});
            skLineSegment(sketch, "E9.12.0.51", {"start": v(65.2, -49.88) * mm, "end": v(65.2, -54.5) * mm});
            skLineSegment(sketch, "E9.12.0.52", {"start": v(52.5, -49.88) * mm, "end": v(52.5, -54.5) * mm});
            skLineSegment(sketch, "E9.12.0.53", {"start": v(103.3, -49.88) * mm, "end": v(103.3, -54.5) * mm});
            skLineSegment(sketch, "E9.12.0.54", {"start": v(-15.62, -54.5) * mm, "end": v(-11, -54.5) * mm});
            skLineSegment(sketch, "E9.12.0.55", {"start": v(111.38, -49.88) * mm, "end": v(111.38, -54.5) * mm});
            skLineSegment(sketch, "E9.12.0.56", {"start": v(60.58, -49.88) * mm, "end": v(60.58, -54.5) * mm});
            skLineSegment(sketch, "E9.12.0.57", {"start": v(85.98, -54.5) * mm, "end": v(90.6, -54.5) * mm});
            skLineSegment(sketch, "E9.12.0.58", {"start": v(35.18, -54.5) * mm, "end": v(39.8, -54.5) * mm});
            skLineSegment(sketch, "E9.12.0.59", {"start": v(9.78, -49.88) * mm, "end": v(9.78, -54.5) * mm});
            skLineSegment(sketch, "E9.12.0.60", {"start": v(-36.4, -49.88) * mm, "end": v(-36.4, -54.5) * mm});
            skLineSegment(sketch, "E9.12.0.61", {"start": v(-41.02, -54.5) * mm, "end": v(-36.4, -54.5) * mm});
            skLineSegment(sketch, "E9.12.0.62", {"start": v(-79.12, -54.5) * mm, "end": v(-74.5, -54.5) * mm});
            skLineSegment(sketch, "E9.12.0.63", {"start": v(-66.42, -54.5) * mm, "end": v(-61.8, -54.5) * mm});
            skLineSegment(sketch, "E9.12.0.64", {"start": v(-66.42, -49.88) * mm, "end": v(-66.42, -54.5) * mm});
            skLineSegment(sketch, "E9.12.0.65", {"start": v(-61.8, -49.88) * mm, "end": v(-61.8, -54.5) * mm});
            skLineSegment(sketch, "E9.12.0.66", {"start": v(-53.72, -49.88) * mm, "end": v(-53.72, -54.5) * mm});
            skLineSegment(sketch, "E9.12.0.67", {"start": v(-2.92, -49.88) * mm, "end": v(-2.92, -54.5) * mm});
            skLineSegment(sketch, "E9.12.0.68", {"start": v(22.48, -49.88) * mm, "end": v(22.48, -54.5) * mm});
            skLineSegment(sketch, "E9.12.0.69", {"start": v(-49.1, -49.88) * mm, "end": v(-49.1, -54.5) * mm});
            skLineSegment(sketch, "E9.12.0.70", {"start": v(1.7, -49.88) * mm, "end": v(1.7, -54.5) * mm});
            skLineSegment(sketch, "E9.12.0.71", {"start": v(77.9, -49.88) * mm, "end": v(77.9, -54.5) * mm});
            skLineSegment(sketch, "E9.12.0.72", {"start": v(27.1, -49.88) * mm, "end": v(27.1, -54.5) * mm});
            skLineSegment(sketch, "E9.12.0.73", {"start": v(-41.02, -49.88) * mm, "end": v(-36.4, -49.88) * mm});
            skLineSegment(sketch, "E9.12.0.74", {"start": v(-28.32, -54.5) * mm, "end": v(-23.7, -54.5) * mm});
            skLineSegment(sketch, "E9.12.0.75", {"start": v(-28.32, -49.88) * mm, "end": v(-23.7, -49.88) * mm});
            skLineSegment(sketch, "E9.12.0.76", {"start": v(22.48, -49.88) * mm, "end": v(27.1, -49.88) * mm});
            skLineSegment(sketch, "E9.12.0.77", {"start": v(73.28, -49.88) * mm, "end": v(77.9, -49.88) * mm});
            skLineSegment(sketch, "E9.12.0.78", {"start": v(-2.92, -49.88) * mm, "end": v(1.7, -49.88) * mm});
            skLineSegment(sketch, "E9.12.0.79", {"start": v(47.88, -49.88) * mm, "end": v(52.5, -49.88) * mm});
            skLineSegment(sketch, "E9.12.0.80", {"start": v(98.68, -49.88) * mm, "end": v(103.3, -49.88) * mm});
            skLineSegment(sketch, "E9.12.0.81", {"start": v(-53.72, -49.88) * mm, "end": v(-49.1, -49.88) * mm});
            skPoint(sketch, "E9.13.0.0", {"position": v(-79.1, -64.89) * mm});
            skPoint(sketch, "E9.13.0.1", {"position": v(88.3, -62.58) * mm});
            skPoint(sketch, "E9.13.0.2", {"position": v(37.5, -62.58) * mm});
            skPoint(sketch, "E9.13.0.3", {"position": v(-51.4, -62.58) * mm});
            skPoint(sketch, "E9.13.0.4", {"position": v(113.7, -62.58) * mm});
            skPoint(sketch, "E9.13.0.5", {"position": v(-64.1, -62.58) * mm});
            skPoint(sketch, "E9.13.0.6", {"position": v(24.8, -62.58) * mm});
            skPoint(sketch, "E9.13.0.7", {"position": v(12.1, -62.58) * mm});
            skLineSegment(sketch, "E9.13.0.8", {"start": v(-76.8, -62.58) * mm, "end": v(-51.4, -62.58) * mm, "construction": true});
            skPoint(sketch, "E9.13.0.9", {"position": v(-76.8, -62.58) * mm});
            skPoint(sketch, "E9.13.0.10", {"position": v(-13.3, -62.58) * mm});
            skPoint(sketch, "E9.13.0.11", {"position": v(50.2, -62.58) * mm});
            skPoint(sketch, "E9.13.0.12", {"position": v(-38.7, -62.58) * mm});
            skPoint(sketch, "E9.13.0.13", {"position": v(62.9, -62.58) * mm});
            skPoint(sketch, "E9.13.0.14", {"position": v(-26, -62.58) * mm});
            skPoint(sketch, "E9.13.0.15", {"position": v(75.6, -62.58) * mm});
            skPoint(sketch, "E9.13.0.16", {"position": v(-0.6, -62.58) * mm});
            skPoint(sketch, "E9.13.0.17", {"position": v(101, -62.58) * mm});
            skLineSegment(sketch, "E9.13.0.18", {"start": v(90.62, -62.58) * mm, "end": v(90.62, -67.2) * mm});
            skLineSegment(sketch, "E9.13.0.19", {"start": v(47.9, -62.58) * mm, "end": v(47.9, -67.2) * mm});
            skLineSegment(sketch, "E9.13.0.20", {"start": v(-28.3, -62.58) * mm, "end": v(-28.3, -67.2) * mm});
            skLineSegment(sketch, "E9.13.0.21", {"start": v(73.3, -62.58) * mm, "end": v(73.3, -67.2) * mm});
            skLineSegment(sketch, "E9.13.0.22", {"start": v(9.8, -67.2) * mm, "end": v(14.42, -67.2) * mm});
            skLineSegment(sketch, "E9.13.0.23", {"start": v(98.7, -62.58) * mm, "end": v(98.7, -67.2) * mm});
            skLineSegment(sketch, "E9.13.0.24", {"start": v(39.82, -62.58) * mm, "end": v(39.82, -67.2) * mm});
            skLineSegment(sketch, "E9.13.0.25", {"start": v(-15.6, -62.58) * mm, "end": v(-15.6, -67.2) * mm});
            skLineSegment(sketch, "E9.13.0.26", {"start": v(60.6, -67.2) * mm, "end": v(65.22, -67.2) * mm});
            skLineSegment(sketch, "E9.13.0.27", {"start": v(35.2, -62.58) * mm, "end": v(35.2, -67.2) * mm});
            skLineSegment(sketch, "E9.13.0.28", {"start": v(86, -62.58) * mm, "end": v(86, -67.2) * mm});
            skLineSegment(sketch, "E9.13.0.29", {"start": v(-53.7, -67.2) * mm, "end": v(-49.08, -67.2) * mm});
            skLineSegment(sketch, "E9.13.0.30", {"start": v(-66.4, -62.58) * mm, "end": v(-61.78, -62.58) * mm});
            skLineSegment(sketch, "E9.13.0.31", {"start": v(111.4, -67.2) * mm, "end": v(116.02, -67.2) * mm});
            skLineSegment(sketch, "E9.13.0.32", {"start": v(-74.48, -62.58) * mm, "end": v(-74.48, -67.2) * mm});
            skLineSegment(sketch, "E9.13.0.33", {"start": v(-79.1, -62.58) * mm, "end": v(-79.1, -67.2) * mm});
            skLineSegment(sketch, "E9.13.0.34", {"start": v(-79.1, -62.58) * mm, "end": v(-74.48, -62.58) * mm});
            skLineSegment(sketch, "E9.13.0.35", {"start": v(-41, -62.58) * mm, "end": v(-41, -67.2) * mm});
            skLineSegment(sketch, "E9.13.0.36", {"start": v(-10.98, -62.58) * mm, "end": v(-10.98, -67.2) * mm});
            skLineSegment(sketch, "E9.13.0.37", {"start": v(-2.9, -67.2) * mm, "end": v(1.72, -67.2) * mm});
            skLineSegment(sketch, "E9.13.0.38", {"start": v(47.9, -67.2) * mm, "end": v(52.52, -67.2) * mm});
            skLineSegment(sketch, "E9.13.0.39", {"start": v(98.7, -67.2) * mm, "end": v(103.32, -67.2) * mm});
            skLineSegment(sketch, "E9.13.0.40", {"start": v(9.8, -62.58) * mm, "end": v(14.42, -62.58) * mm});
            skLineSegment(sketch, "E9.13.0.41", {"start": v(14.42, -62.58) * mm, "end": v(14.42, -67.2) * mm});
            skLineSegment(sketch, "E9.13.0.42", {"start": v(22.5, -67.2) * mm, "end": v(27.12, -67.2) * mm});
            skLineSegment(sketch, "E9.13.0.43", {"start": v(73.3, -67.2) * mm, "end": v(77.92, -67.2) * mm});
            skLineSegment(sketch, "E9.13.0.44", {"start": v(116.02, -62.58) * mm, "end": v(116.02, -67.2) * mm});
            skLineSegment(sketch, "E9.13.0.45", {"start": v(60.6, -62.58) * mm, "end": v(65.22, -62.58) * mm});
            skLineSegment(sketch, "E9.13.0.46", {"start": v(111.4, -62.58) * mm, "end": v(116.02, -62.58) * mm});
            skLineSegment(sketch, "E9.13.0.47", {"start": v(-15.6, -62.58) * mm, "end": v(-10.98, -62.58) * mm});
            skLineSegment(sketch, "E9.13.0.48", {"start": v(35.2, -62.58) * mm, "end": v(39.82, -62.58) * mm});
            skLineSegment(sketch, "E9.13.0.49", {"start": v(-23.68, -62.58) * mm, "end": v(-23.68, -67.2) * mm});
            skLineSegment(sketch, "E9.13.0.50", {"start": v(86, -62.58) * mm, "end": v(90.62, -62.58) * mm});
            skLineSegment(sketch, "E9.13.0.51", {"start": v(65.22, -62.58) * mm, "end": v(65.22, -67.2) * mm});
            skLineSegment(sketch, "E9.13.0.52", {"start": v(52.52, -62.58) * mm, "end": v(52.52, -67.2) * mm});
            skLineSegment(sketch, "E9.13.0.53", {"start": v(103.32, -62.58) * mm, "end": v(103.32, -67.2) * mm});
            skLineSegment(sketch, "E9.13.0.54", {"start": v(-15.6, -67.2) * mm, "end": v(-10.98, -67.2) * mm});
            skLineSegment(sketch, "E9.13.0.55", {"start": v(111.4, -62.58) * mm, "end": v(111.4, -67.2) * mm});
            skLineSegment(sketch, "E9.13.0.56", {"start": v(60.6, -62.58) * mm, "end": v(60.6, -67.2) * mm});
            skLineSegment(sketch, "E9.13.0.57", {"start": v(86, -67.2) * mm, "end": v(90.62, -67.2) * mm});
            skLineSegment(sketch, "E9.13.0.58", {"start": v(35.2, -67.2) * mm, "end": v(39.82, -67.2) * mm});
            skLineSegment(sketch, "E9.13.0.59", {"start": v(9.8, -62.58) * mm, "end": v(9.8, -67.2) * mm});
            skLineSegment(sketch, "E9.13.0.60", {"start": v(-36.38, -62.58) * mm, "end": v(-36.38, -67.2) * mm});
            skLineSegment(sketch, "E9.13.0.61", {"start": v(-41, -67.2) * mm, "end": v(-36.38, -67.2) * mm});
            skLineSegment(sketch, "E9.13.0.62", {"start": v(-79.1, -67.2) * mm, "end": v(-74.48, -67.2) * mm});
            skLineSegment(sketch, "E9.13.0.63", {"start": v(-66.4, -67.2) * mm, "end": v(-61.78, -67.2) * mm});
            skLineSegment(sketch, "E9.13.0.64", {"start": v(-66.4, -62.58) * mm, "end": v(-66.4, -67.2) * mm});
            skLineSegment(sketch, "E9.13.0.65", {"start": v(-61.78, -62.58) * mm, "end": v(-61.78, -67.2) * mm});
            skLineSegment(sketch, "E9.13.0.66", {"start": v(-53.7, -62.58) * mm, "end": v(-53.7, -67.2) * mm});
            skLineSegment(sketch, "E9.13.0.67", {"start": v(-2.9, -62.58) * mm, "end": v(-2.9, -67.2) * mm});
            skLineSegment(sketch, "E9.13.0.68", {"start": v(22.5, -62.58) * mm, "end": v(22.5, -67.2) * mm});
            skLineSegment(sketch, "E9.13.0.69", {"start": v(-49.08, -62.58) * mm, "end": v(-49.08, -67.2) * mm});
            skLineSegment(sketch, "E9.13.0.70", {"start": v(1.72, -62.58) * mm, "end": v(1.72, -67.2) * mm});
            skLineSegment(sketch, "E9.13.0.71", {"start": v(77.92, -62.58) * mm, "end": v(77.92, -67.2) * mm});
            skLineSegment(sketch, "E9.13.0.72", {"start": v(27.12, -62.58) * mm, "end": v(27.12, -67.2) * mm});
            skLineSegment(sketch, "E9.13.0.73", {"start": v(-41, -62.58) * mm, "end": v(-36.38, -62.58) * mm});
            skLineSegment(sketch, "E9.13.0.74", {"start": v(-28.3, -67.2) * mm, "end": v(-23.68, -67.2) * mm});
            skLineSegment(sketch, "E9.13.0.75", {"start": v(-28.3, -62.58) * mm, "end": v(-23.68, -62.58) * mm});
            skLineSegment(sketch, "E9.13.0.76", {"start": v(22.5, -62.58) * mm, "end": v(27.12, -62.58) * mm});
            skLineSegment(sketch, "E9.13.0.77", {"start": v(73.3, -62.58) * mm, "end": v(77.92, -62.58) * mm});
            skLineSegment(sketch, "E9.13.0.78", {"start": v(-2.9, -62.58) * mm, "end": v(1.72, -62.58) * mm});
            skLineSegment(sketch, "E9.13.0.79", {"start": v(47.9, -62.58) * mm, "end": v(52.52, -62.58) * mm});
            skLineSegment(sketch, "E9.13.0.80", {"start": v(98.7, -62.58) * mm, "end": v(103.32, -62.58) * mm});
            skLineSegment(sketch, "E9.13.0.81", {"start": v(-53.7, -62.58) * mm, "end": v(-49.08, -62.58) * mm});
            skPoint(sketch, "E9.14.0.0", {"position": v(-79.09, -77.59) * mm});
            skPoint(sketch, "E9.14.0.1", {"position": v(88.32, -75.28) * mm});
            skPoint(sketch, "E9.14.0.2", {"position": v(37.52, -75.28) * mm});
            skPoint(sketch, "E9.14.0.3", {"position": v(-51.38, -75.28) * mm});
            skPoint(sketch, "E9.14.0.4", {"position": v(113.72, -75.28) * mm});
            skPoint(sketch, "E9.14.0.5", {"position": v(-64.08, -75.28) * mm});
            skPoint(sketch, "E9.14.0.6", {"position": v(24.82, -75.28) * mm});
            skPoint(sketch, "E9.14.0.7", {"position": v(12.12, -75.28) * mm});
            skLineSegment(sketch, "E9.14.0.8", {"start": v(-76.78, -75.28) * mm, "end": v(-51.38, -75.28) * mm, "construction": true});
            skPoint(sketch, "E9.14.0.9", {"position": v(-76.78, -75.28) * mm});
            skPoint(sketch, "E9.14.0.10", {"position": v(-13.28, -75.28) * mm});
            skPoint(sketch, "E9.14.0.11", {"position": v(50.22, -75.28) * mm});
            skPoint(sketch, "E9.14.0.12", {"position": v(-38.68, -75.28) * mm});
            skPoint(sketch, "E9.14.0.13", {"position": v(62.92, -75.28) * mm});
            skPoint(sketch, "E9.14.0.14", {"position": v(-25.98, -75.28) * mm});
            skPoint(sketch, "E9.14.0.15", {"position": v(75.62, -75.28) * mm});
            skPoint(sketch, "E9.14.0.16", {"position": v(-0.58, -75.28) * mm});
            skPoint(sketch, "E9.14.0.17", {"position": v(101.02, -75.28) * mm});
            skLineSegment(sketch, "E9.14.0.18", {"start": v(90.63, -75.28) * mm, "end": v(90.63, -79.9) * mm});
            skLineSegment(sketch, "E9.14.0.19", {"start": v(47.91, -75.28) * mm, "end": v(47.91, -79.9) * mm});
            skLineSegment(sketch, "E9.14.0.20", {"start": v(-28.29, -75.28) * mm, "end": v(-28.29, -79.9) * mm});
            skLineSegment(sketch, "E9.14.0.21", {"start": v(73.31, -75.28) * mm, "end": v(73.31, -79.9) * mm});
            skLineSegment(sketch, "E9.14.0.22", {"start": v(9.81, -79.9) * mm, "end": v(14.43, -79.9) * mm});
            skLineSegment(sketch, "E9.14.0.23", {"start": v(98.71, -75.28) * mm, "end": v(98.71, -79.9) * mm});
            skLineSegment(sketch, "E9.14.0.24", {"start": v(39.83, -75.28) * mm, "end": v(39.83, -79.9) * mm});
            skLineSegment(sketch, "E9.14.0.25", {"start": v(-15.59, -75.28) * mm, "end": v(-15.59, -79.9) * mm});
            skLineSegment(sketch, "E9.14.0.26", {"start": v(60.61, -79.9) * mm, "end": v(65.23, -79.9) * mm});
            skLineSegment(sketch, "E9.14.0.27", {"start": v(35.21, -75.28) * mm, "end": v(35.21, -79.9) * mm});
            skLineSegment(sketch, "E9.14.0.28", {"start": v(86.01, -75.28) * mm, "end": v(86.01, -79.9) * mm});
            skLineSegment(sketch, "E9.14.0.29", {"start": v(-53.69, -79.9) * mm, "end": v(-49.07, -79.9) * mm});
            skLineSegment(sketch, "E9.14.0.30", {"start": v(-66.39, -75.28) * mm, "end": v(-61.77, -75.28) * mm});
            skLineSegment(sketch, "E9.14.0.31", {"start": v(111.41, -79.9) * mm, "end": v(116.03, -79.9) * mm});
            skLineSegment(sketch, "E9.14.0.32", {"start": v(-74.47, -75.28) * mm, "end": v(-74.47, -79.9) * mm});
            skLineSegment(sketch, "E9.14.0.33", {"start": v(-79.09, -75.28) * mm, "end": v(-79.09, -79.9) * mm});
            skLineSegment(sketch, "E9.14.0.34", {"start": v(-79.09, -75.28) * mm, "end": v(-74.47, -75.28) * mm});
            skLineSegment(sketch, "E9.14.0.35", {"start": v(-40.99, -75.28) * mm, "end": v(-40.99, -79.9) * mm});
            skLineSegment(sketch, "E9.14.0.36", {"start": v(-10.97, -75.28) * mm, "end": v(-10.97, -79.9) * mm});
            skLineSegment(sketch, "E9.14.0.37", {"start": v(-2.89, -79.9) * mm, "end": v(1.73, -79.9) * mm});
            skLineSegment(sketch, "E9.14.0.38", {"start": v(47.91, -79.9) * mm, "end": v(52.53, -79.9) * mm});
            skLineSegment(sketch, "E9.14.0.39", {"start": v(98.71, -79.9) * mm, "end": v(103.33, -79.9) * mm});
            skLineSegment(sketch, "E9.14.0.40", {"start": v(9.81, -75.28) * mm, "end": v(14.43, -75.28) * mm});
            skLineSegment(sketch, "E9.14.0.41", {"start": v(14.43, -75.28) * mm, "end": v(14.43, -79.9) * mm});
            skLineSegment(sketch, "E9.14.0.42", {"start": v(22.51, -79.9) * mm, "end": v(27.13, -79.9) * mm});
            skLineSegment(sketch, "E9.14.0.43", {"start": v(73.31, -79.9) * mm, "end": v(77.93, -79.9) * mm});
            skLineSegment(sketch, "E9.14.0.44", {"start": v(116.03, -75.28) * mm, "end": v(116.03, -79.9) * mm});
            skLineSegment(sketch, "E9.14.0.45", {"start": v(60.61, -75.28) * mm, "end": v(65.23, -75.28) * mm});
            skLineSegment(sketch, "E9.14.0.46", {"start": v(111.41, -75.28) * mm, "end": v(116.03, -75.28) * mm});
            skLineSegment(sketch, "E9.14.0.47", {"start": v(-15.59, -75.28) * mm, "end": v(-10.97, -75.28) * mm});
            skLineSegment(sketch, "E9.14.0.48", {"start": v(35.21, -75.28) * mm, "end": v(39.83, -75.28) * mm});
            skLineSegment(sketch, "E9.14.0.49", {"start": v(-23.67, -75.28) * mm, "end": v(-23.67, -79.9) * mm});
            skLineSegment(sketch, "E9.14.0.50", {"start": v(86.01, -75.28) * mm, "end": v(90.63, -75.28) * mm});
            skLineSegment(sketch, "E9.14.0.51", {"start": v(65.23, -75.28) * mm, "end": v(65.23, -79.9) * mm});
            skLineSegment(sketch, "E9.14.0.52", {"start": v(52.53, -75.28) * mm, "end": v(52.53, -79.9) * mm});
            skLineSegment(sketch, "E9.14.0.53", {"start": v(103.33, -75.28) * mm, "end": v(103.33, -79.9) * mm});
            skLineSegment(sketch, "E9.14.0.54", {"start": v(-15.59, -79.9) * mm, "end": v(-10.97, -79.9) * mm});
            skLineSegment(sketch, "E9.14.0.55", {"start": v(111.41, -75.28) * mm, "end": v(111.41, -79.9) * mm});
            skLineSegment(sketch, "E9.14.0.56", {"start": v(60.61, -75.28) * mm, "end": v(60.61, -79.9) * mm});
            skLineSegment(sketch, "E9.14.0.57", {"start": v(86.01, -79.9) * mm, "end": v(90.63, -79.9) * mm});
            skLineSegment(sketch, "E9.14.0.58", {"start": v(35.21, -79.9) * mm, "end": v(39.83, -79.9) * mm});
            skLineSegment(sketch, "E9.14.0.59", {"start": v(9.81, -75.28) * mm, "end": v(9.81, -79.9) * mm});
            skLineSegment(sketch, "E9.14.0.60", {"start": v(-36.37, -75.28) * mm, "end": v(-36.37, -79.9) * mm});
            skLineSegment(sketch, "E9.14.0.61", {"start": v(-40.99, -79.9) * mm, "end": v(-36.37, -79.9) * mm});
            skLineSegment(sketch, "E9.14.0.62", {"start": v(-79.09, -79.9) * mm, "end": v(-74.47, -79.9) * mm});
            skLineSegment(sketch, "E9.14.0.63", {"start": v(-66.39, -79.9) * mm, "end": v(-61.77, -79.9) * mm});
            skLineSegment(sketch, "E9.14.0.64", {"start": v(-66.39, -75.28) * mm, "end": v(-66.39, -79.9) * mm});
            skLineSegment(sketch, "E9.14.0.65", {"start": v(-61.77, -75.28) * mm, "end": v(-61.77, -79.9) * mm});
            skLineSegment(sketch, "E9.14.0.66", {"start": v(-53.69, -75.28) * mm, "end": v(-53.69, -79.9) * mm});
            skLineSegment(sketch, "E9.14.0.67", {"start": v(-2.89, -75.28) * mm, "end": v(-2.89, -79.9) * mm});
            skLineSegment(sketch, "E9.14.0.68", {"start": v(22.51, -75.28) * mm, "end": v(22.51, -79.9) * mm});
            skLineSegment(sketch, "E9.14.0.69", {"start": v(-49.07, -75.28) * mm, "end": v(-49.07, -79.9) * mm});
            skLineSegment(sketch, "E9.14.0.70", {"start": v(1.73, -75.28) * mm, "end": v(1.73, -79.9) * mm});
            skLineSegment(sketch, "E9.14.0.71", {"start": v(77.93, -75.28) * mm, "end": v(77.93, -79.9) * mm});
            skLineSegment(sketch, "E9.14.0.72", {"start": v(27.13, -75.28) * mm, "end": v(27.13, -79.9) * mm});
            skLineSegment(sketch, "E9.14.0.73", {"start": v(-40.99, -75.28) * mm, "end": v(-36.37, -75.28) * mm});
            skLineSegment(sketch, "E9.14.0.74", {"start": v(-28.29, -79.9) * mm, "end": v(-23.67, -79.9) * mm});
            skLineSegment(sketch, "E9.14.0.75", {"start": v(-28.29, -75.28) * mm, "end": v(-23.67, -75.28) * mm});
            skLineSegment(sketch, "E9.14.0.76", {"start": v(22.51, -75.28) * mm, "end": v(27.13, -75.28) * mm});
            skLineSegment(sketch, "E9.14.0.77", {"start": v(73.31, -75.28) * mm, "end": v(77.93, -75.28) * mm});
            skLineSegment(sketch, "E9.14.0.78", {"start": v(-2.89, -75.28) * mm, "end": v(1.73, -75.28) * mm});
            skLineSegment(sketch, "E9.14.0.79", {"start": v(47.91, -75.28) * mm, "end": v(52.53, -75.28) * mm});
            skLineSegment(sketch, "E9.14.0.80", {"start": v(98.71, -75.28) * mm, "end": v(103.33, -75.28) * mm});
            skLineSegment(sketch, "E9.14.0.81", {"start": v(-53.69, -75.28) * mm, "end": v(-49.07, -75.28) * mm});
            skPoint(sketch, "E9.15.0.0", {"position": v(-79.08, -90.29) * mm});
            skPoint(sketch, "E9.15.0.1", {"position": v(88.33, -87.98) * mm});
            skPoint(sketch, "E9.15.0.2", {"position": v(37.53, -87.98) * mm});
            skPoint(sketch, "E9.15.0.3", {"position": v(-51.37, -87.98) * mm});
            skPoint(sketch, "E9.15.0.4", {"position": v(113.73, -87.98) * mm});
            skPoint(sketch, "E9.15.0.5", {"position": v(-64.07, -87.98) * mm});
            skPoint(sketch, "E9.15.0.6", {"position": v(24.83, -87.98) * mm});
            skPoint(sketch, "E9.15.0.7", {"position": v(12.13, -87.98) * mm});
            skLineSegment(sketch, "E9.15.0.8", {"start": v(-76.77, -87.98) * mm, "end": v(-51.37, -87.98) * mm, "construction": true});
            skPoint(sketch, "E9.15.0.9", {"position": v(-76.77, -87.98) * mm});
            skPoint(sketch, "E9.15.0.10", {"position": v(-13.27, -87.98) * mm});
            skPoint(sketch, "E9.15.0.11", {"position": v(50.23, -87.98) * mm});
            skPoint(sketch, "E9.15.0.12", {"position": v(-38.67, -87.98) * mm});
            skPoint(sketch, "E9.15.0.13", {"position": v(62.93, -87.98) * mm});
            skPoint(sketch, "E9.15.0.14", {"position": v(-25.97, -87.98) * mm});
            skPoint(sketch, "E9.15.0.15", {"position": v(75.63, -87.98) * mm});
            skPoint(sketch, "E9.15.0.16", {"position": v(-0.57, -87.98) * mm});
            skPoint(sketch, "E9.15.0.17", {"position": v(101.03, -87.98) * mm});
            skLineSegment(sketch, "E9.15.0.18", {"start": v(90.65, -87.98) * mm, "end": v(90.65, -92.6) * mm});
            skLineSegment(sketch, "E9.15.0.19", {"start": v(47.92, -87.98) * mm, "end": v(47.92, -92.6) * mm});
            skLineSegment(sketch, "E9.15.0.20", {"start": v(-28.28, -87.98) * mm, "end": v(-28.28, -92.6) * mm});
            skLineSegment(sketch, "E9.15.0.21", {"start": v(73.32, -87.98) * mm, "end": v(73.32, -92.6) * mm});
            skLineSegment(sketch, "E9.15.0.22", {"start": v(9.82, -92.6) * mm, "end": v(14.45, -92.6) * mm});
            skLineSegment(sketch, "E9.15.0.23", {"start": v(98.72, -87.98) * mm, "end": v(98.72, -92.6) * mm});
            skLineSegment(sketch, "E9.15.0.24", {"start": v(39.85, -87.98) * mm, "end": v(39.85, -92.6) * mm});
            skLineSegment(sketch, "E9.15.0.25", {"start": v(-15.58, -87.98) * mm, "end": v(-15.58, -92.6) * mm});
            skLineSegment(sketch, "E9.15.0.26", {"start": v(60.62, -92.6) * mm, "end": v(65.25, -92.6) * mm});
            skLineSegment(sketch, "E9.15.0.27", {"start": v(35.22, -87.98) * mm, "end": v(35.22, -92.6) * mm});
            skLineSegment(sketch, "E9.15.0.28", {"start": v(86.02, -87.98) * mm, "end": v(86.02, -92.6) * mm});
            skLineSegment(sketch, "E9.15.0.29", {"start": v(-53.68, -92.6) * mm, "end": v(-49.05, -92.6) * mm});
            skLineSegment(sketch, "E9.15.0.30", {"start": v(-66.38, -87.98) * mm, "end": v(-61.75, -87.98) * mm});
            skLineSegment(sketch, "E9.15.0.31", {"start": v(111.42, -92.6) * mm, "end": v(116.05, -92.6) * mm});
            skLineSegment(sketch, "E9.15.0.32", {"start": v(-74.45, -87.98) * mm, "end": v(-74.45, -92.6) * mm});
            skLineSegment(sketch, "E9.15.0.33", {"start": v(-79.08, -87.98) * mm, "end": v(-79.08, -92.6) * mm});
            skLineSegment(sketch, "E9.15.0.34", {"start": v(-79.08, -87.98) * mm, "end": v(-74.45, -87.98) * mm});
            skLineSegment(sketch, "E9.15.0.35", {"start": v(-40.98, -87.98) * mm, "end": v(-40.98, -92.6) * mm});
            skLineSegment(sketch, "E9.15.0.36", {"start": v(-10.95, -87.98) * mm, "end": v(-10.95, -92.6) * mm});
            skLineSegment(sketch, "E9.15.0.37", {"start": v(-2.88, -92.6) * mm, "end": v(1.75, -92.6) * mm});
            skLineSegment(sketch, "E9.15.0.38", {"start": v(47.92, -92.6) * mm, "end": v(52.55, -92.6) * mm});
            skLineSegment(sketch, "E9.15.0.39", {"start": v(98.72, -92.6) * mm, "end": v(103.35, -92.6) * mm});
            skLineSegment(sketch, "E9.15.0.40", {"start": v(9.82, -87.98) * mm, "end": v(14.45, -87.98) * mm});
            skLineSegment(sketch, "E9.15.0.41", {"start": v(14.45, -87.98) * mm, "end": v(14.45, -92.6) * mm});
            skLineSegment(sketch, "E9.15.0.42", {"start": v(22.52, -92.6) * mm, "end": v(27.15, -92.6) * mm});
            skLineSegment(sketch, "E9.15.0.43", {"start": v(73.32, -92.6) * mm, "end": v(77.95, -92.6) * mm});
            skLineSegment(sketch, "E9.15.0.44", {"start": v(116.05, -87.98) * mm, "end": v(116.05, -92.6) * mm});
            skLineSegment(sketch, "E9.15.0.45", {"start": v(60.62, -87.98) * mm, "end": v(65.25, -87.98) * mm});
            skLineSegment(sketch, "E9.15.0.46", {"start": v(111.42, -87.98) * mm, "end": v(116.05, -87.98) * mm});
            skLineSegment(sketch, "E9.15.0.47", {"start": v(-15.58, -87.98) * mm, "end": v(-10.95, -87.98) * mm});
            skLineSegment(sketch, "E9.15.0.48", {"start": v(35.22, -87.98) * mm, "end": v(39.85, -87.98) * mm});
            skLineSegment(sketch, "E9.15.0.49", {"start": v(-23.65, -87.98) * mm, "end": v(-23.65, -92.6) * mm});
            skLineSegment(sketch, "E9.15.0.50", {"start": v(86.02, -87.98) * mm, "end": v(90.65, -87.98) * mm});
            skLineSegment(sketch, "E9.15.0.51", {"start": v(65.25, -87.98) * mm, "end": v(65.25, -92.6) * mm});
            skLineSegment(sketch, "E9.15.0.52", {"start": v(52.55, -87.98) * mm, "end": v(52.55, -92.6) * mm});
            skLineSegment(sketch, "E9.15.0.53", {"start": v(103.35, -87.98) * mm, "end": v(103.35, -92.6) * mm});
            skLineSegment(sketch, "E9.15.0.54", {"start": v(-15.58, -92.6) * mm, "end": v(-10.95, -92.6) * mm});
            skLineSegment(sketch, "E9.15.0.55", {"start": v(111.42, -87.98) * mm, "end": v(111.42, -92.6) * mm});
            skLineSegment(sketch, "E9.15.0.56", {"start": v(60.62, -87.98) * mm, "end": v(60.62, -92.6) * mm});
            skLineSegment(sketch, "E9.15.0.57", {"start": v(86.02, -92.6) * mm, "end": v(90.65, -92.6) * mm});
            skLineSegment(sketch, "E9.15.0.58", {"start": v(35.22, -92.6) * mm, "end": v(39.85, -92.6) * mm});
            skLineSegment(sketch, "E9.15.0.59", {"start": v(9.82, -87.98) * mm, "end": v(9.82, -92.6) * mm});
            skLineSegment(sketch, "E9.15.0.60", {"start": v(-36.35, -87.98) * mm, "end": v(-36.35, -92.6) * mm});
            skLineSegment(sketch, "E9.15.0.61", {"start": v(-40.98, -92.6) * mm, "end": v(-36.35, -92.6) * mm});
            skLineSegment(sketch, "E9.15.0.62", {"start": v(-79.08, -92.6) * mm, "end": v(-74.45, -92.6) * mm});
            skLineSegment(sketch, "E9.15.0.63", {"start": v(-66.38, -92.6) * mm, "end": v(-61.75, -92.6) * mm});
            skLineSegment(sketch, "E9.15.0.64", {"start": v(-66.38, -87.98) * mm, "end": v(-66.38, -92.6) * mm});
            skLineSegment(sketch, "E9.15.0.65", {"start": v(-61.75, -87.98) * mm, "end": v(-61.75, -92.6) * mm});
            skLineSegment(sketch, "E9.15.0.66", {"start": v(-53.68, -87.98) * mm, "end": v(-53.68, -92.6) * mm});
            skLineSegment(sketch, "E9.15.0.67", {"start": v(-2.88, -87.98) * mm, "end": v(-2.88, -92.6) * mm});
            skLineSegment(sketch, "E9.15.0.68", {"start": v(22.52, -87.98) * mm, "end": v(22.52, -92.6) * mm});
            skLineSegment(sketch, "E9.15.0.69", {"start": v(-49.05, -87.98) * mm, "end": v(-49.05, -92.6) * mm});
            skLineSegment(sketch, "E9.15.0.70", {"start": v(1.75, -87.98) * mm, "end": v(1.75, -92.6) * mm});
            skLineSegment(sketch, "E9.15.0.71", {"start": v(77.95, -87.98) * mm, "end": v(77.95, -92.6) * mm});
            skLineSegment(sketch, "E9.15.0.72", {"start": v(27.15, -87.98) * mm, "end": v(27.15, -92.6) * mm});
            skLineSegment(sketch, "E9.15.0.73", {"start": v(-40.98, -87.98) * mm, "end": v(-36.35, -87.98) * mm});
            skLineSegment(sketch, "E9.15.0.74", {"start": v(-28.28, -92.6) * mm, "end": v(-23.65, -92.6) * mm});
            skLineSegment(sketch, "E9.15.0.75", {"start": v(-28.28, -87.98) * mm, "end": v(-23.65, -87.98) * mm});
            skLineSegment(sketch, "E9.15.0.76", {"start": v(22.52, -87.98) * mm, "end": v(27.15, -87.98) * mm});
            skLineSegment(sketch, "E9.15.0.77", {"start": v(73.32, -87.98) * mm, "end": v(77.95, -87.98) * mm});
            skLineSegment(sketch, "E9.15.0.78", {"start": v(-2.88, -87.98) * mm, "end": v(1.75, -87.98) * mm});
            skLineSegment(sketch, "E9.15.0.79", {"start": v(47.92, -87.98) * mm, "end": v(52.55, -87.98) * mm});
            skLineSegment(sketch, "E9.15.0.80", {"start": v(98.72, -87.98) * mm, "end": v(103.35, -87.98) * mm});
            skLineSegment(sketch, "E9.15.0.81", {"start": v(-53.68, -87.98) * mm, "end": v(-49.05, -87.98) * mm});
            skLineSegment(sketch, "E9.direction1", {"start": v(-79.27, 100.21) * mm, "end": v(-79.25, 87.51) * mm, "construction": true});
            skSolve(sketch);
        }
        {
            var Q0;
            Q0=makeQuery(id+"F0.imprint","IMPRINT",FACE,{"disambiguationData":[TD([[makeQuery(id+"F0.imprint","IMPRINT",EDGE,{"derivedFrom":sQuery(id+"F0.wireOp",EDGE,"E0.bottom")}),-1.0]])]});
            extrude(context, id + "F1", {"entities" : qUnion([Q0]), "depth" : 3.17 * mm});
        }
    });
